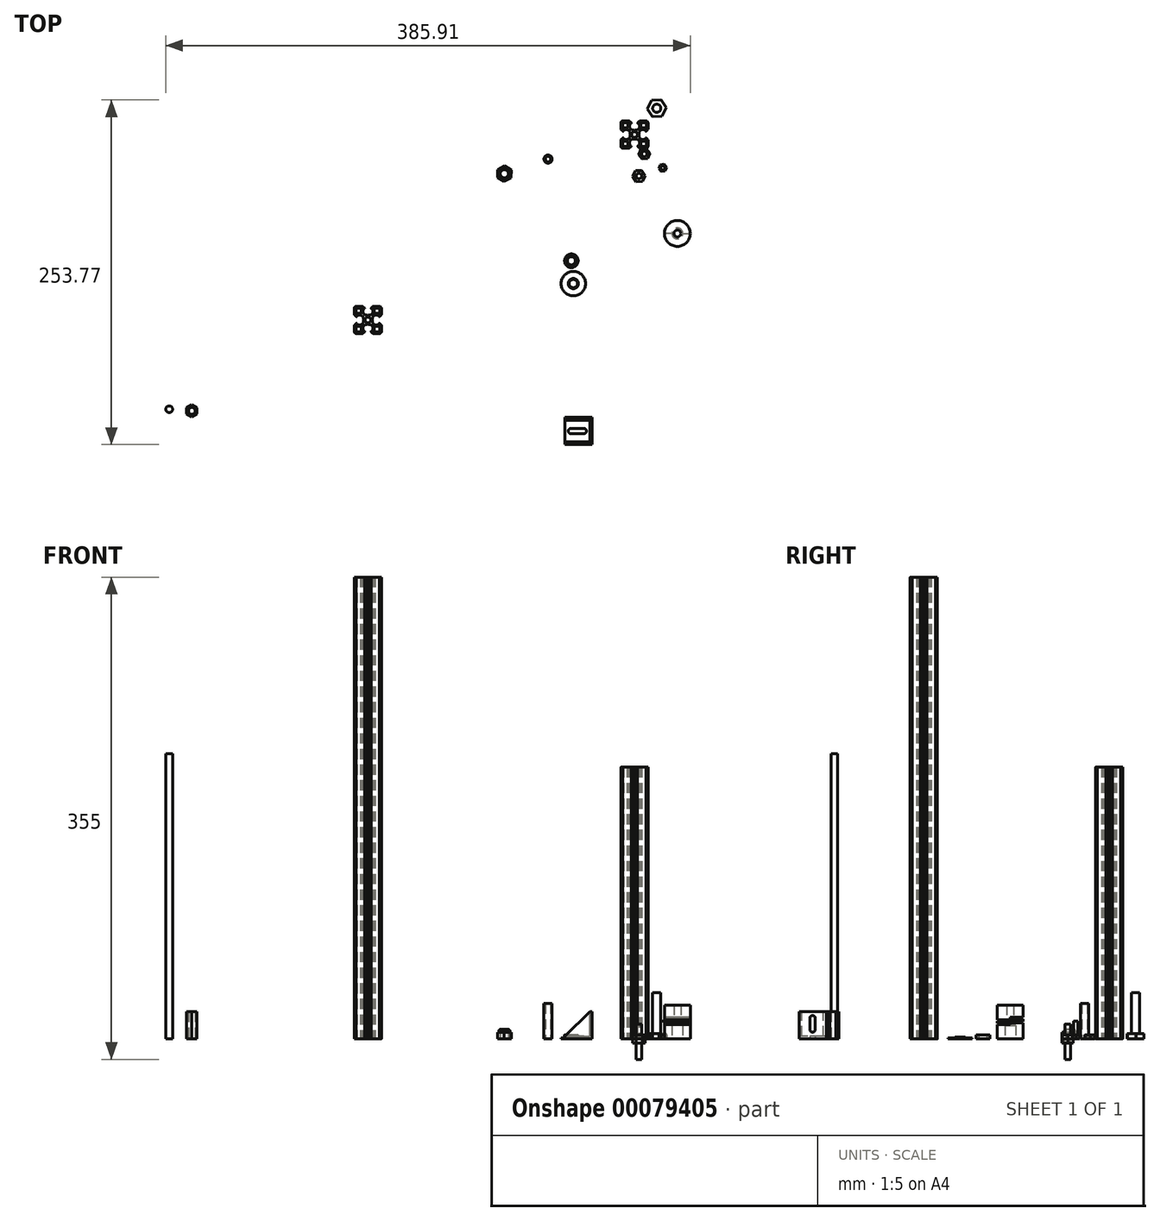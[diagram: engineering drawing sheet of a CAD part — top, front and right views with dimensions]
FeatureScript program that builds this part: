
annotation { "Feature Type Name" : "Feature", "Feature Type Description" : "" }
export const myFeature = defineFeature(function(context is Context, id is Id, definition is map)
    precondition{}
    {
        {
            var Q0;
            Q0=qCreatedBy(makeId("Top.planeOp"),FACE);
            var sketch = newSketch(context, id + "F0", { "sketchPlane" : qUnion([Q0])});
            skLineSegment(sketch, "E0", {"start": v(-9.77, 3.7) * mm, "end": v(-8.49, 2.4) * mm});
            skArc(sketch, "E1", {"start": v(-8.49, 2.4) * mm, "mid": v(-8.27, 2.36) * mm, "end": v(-8.14, 2.54) * mm});
            skLineSegment(sketch, "E2", {"start": v(-8.14, 2.54) * mm, "end": v(-8.14, 3.6) * mm});
            skLineSegment(sketch, "E3", {"start": v(-8.14, 3.6) * mm, "end": v(-5.03, 3.6) * mm});
            skLineSegment(sketch, "E4", {"start": v(-5.03, 3.6) * mm, "end": v(-3.4, 1.97) * mm});
            skLineSegment(sketch, "E5", {"start": v(-3.4, 1.97) * mm, "end": v(-3.4, 0.38) * mm});
            skLineSegment(sketch, "E6", {"start": v(-3.4, 0.38) * mm, "end": v(-3.02, 0) * mm});
            skLineSegment(sketch, "E7", {"start": v(-3.4, -0.38) * mm, "end": v(-3.02, 0) * mm});
            skLineSegment(sketch, "E8", {"start": v(-3.4, -1.97) * mm, "end": v(-3.4, -0.38) * mm});
            skLineSegment(sketch, "E9", {"start": v(-5.03, -3.6) * mm, "end": v(-3.4, -1.97) * mm});
            skLineSegment(sketch, "E10", {"start": v(-8.14, -3.6) * mm, "end": v(-5.03, -3.6) * mm});
            skLineSegment(sketch, "E11", {"start": v(-8.14, -2.54) * mm, "end": v(-8.14, -3.6) * mm});
            skArc(sketch, "E12", {"start": v(-8.49, -2.4) * mm, "mid": v(-8.27, -2.36) * mm, "end": v(-8.14, -2.54) * mm});
            skLineSegment(sketch, "E13", {"start": v(-9.77, -3.7) * mm, "end": v(-8.49, -2.4) * mm});
            skArc(sketch, "E14", {"start": v(-10, -4.25) * mm, "mid": v(-9.94, -3.95) * mm, "end": v(-9.77, -3.7) * mm});
            skLineSegment(sketch, "E15", {"start": v(-10, -8.58) * mm, "end": v(-10, -4.25) * mm});
            skArc(sketch, "E16", {"start": v(-8.6, -10) * mm, "mid": v(-9.57, -9.56) * mm, "end": v(-10, -8.58) * mm});
            skLineSegment(sketch, "E17", {"start": v(-4.04, -10) * mm, "end": v(-8.6, -10) * mm});
            skArc(sketch, "E18", {"start": v(-3.48, -9.77) * mm, "mid": v(-3.74, -9.94) * mm, "end": v(-4.04, -10) * mm});
            skLineSegment(sketch, "E19", {"start": v(-2.37, -8.66) * mm, "end": v(-3.48, -9.77) * mm});
            skArc(sketch, "E20", {"start": v(-2.55, -8.23) * mm, "mid": v(-2.32, -8.39) * mm, "end": v(-2.37, -8.66) * mm});
            skLineSegment(sketch, "E21", {"start": v(-3.6, -8.23) * mm, "end": v(-2.55, -8.23) * mm});
            skLineSegment(sketch, "E22", {"start": v(-3.6, -5.03) * mm, "end": v(-3.6, -8.23) * mm});
            skLineSegment(sketch, "E23", {"start": v(-2, -3.43) * mm, "end": v(-3.6, -5.03) * mm});
            skLineSegment(sketch, "E24", {"start": v(-0.3, -3.43) * mm, "end": v(-2, -3.43) * mm});
            skLineSegment(sketch, "E25", {"start": v(0, -3.18) * mm, "end": v(-0.3, -3.43) * mm});
            skLineSegment(sketch, "E26", {"start": v(0, -3.18) * mm, "end": v(0.3, -3.43) * mm});
            skLineSegment(sketch, "E27", {"start": v(0.3, -3.43) * mm, "end": v(2, -3.43) * mm});
            skLineSegment(sketch, "E28", {"start": v(2, -3.43) * mm, "end": v(3.6, -5.03) * mm});
            skLineSegment(sketch, "E29", {"start": v(3.6, -5.03) * mm, "end": v(3.6, -8.23) * mm});
            skLineSegment(sketch, "E30", {"start": v(3.6, -8.23) * mm, "end": v(2.55, -8.23) * mm});
            skArc(sketch, "E31", {"start": v(2.55, -8.23) * mm, "mid": v(2.32, -8.39) * mm, "end": v(2.37, -8.66) * mm});
            skLineSegment(sketch, "E32", {"start": v(2.37, -8.66) * mm, "end": v(3.48, -9.77) * mm});
            skArc(sketch, "E33", {"start": v(3.48, -9.77) * mm, "mid": v(3.74, -9.94) * mm, "end": v(4.04, -10) * mm});
            skLineSegment(sketch, "E34", {"start": v(4.04, -10) * mm, "end": v(8.6, -10) * mm});
            skArc(sketch, "E35", {"start": v(8.6, -10) * mm, "mid": v(9.57, -9.56) * mm, "end": v(10, -8.58) * mm});
            skLineSegment(sketch, "E36", {"start": v(10, -8.58) * mm, "end": v(10, -4.25) * mm});
            skArc(sketch, "E37", {"start": v(10, -4.25) * mm, "mid": v(9.94, -3.95) * mm, "end": v(9.77, -3.7) * mm});
            skLineSegment(sketch, "E38", {"start": v(9.77, -3.7) * mm, "end": v(8.49, -2.4) * mm});
            skArc(sketch, "E39", {"start": v(8.49, -2.4) * mm, "mid": v(8.27, -2.36) * mm, "end": v(8.14, -2.54) * mm});
            skLineSegment(sketch, "E40", {"start": v(8.14, -2.54) * mm, "end": v(8.14, -3.6) * mm});
            skLineSegment(sketch, "E41", {"start": v(8.14, -3.6) * mm, "end": v(5.03, -3.6) * mm});
            skLineSegment(sketch, "E42", {"start": v(5.03, -3.6) * mm, "end": v(3.4, -1.97) * mm});
            skLineSegment(sketch, "E43", {"start": v(3.4, -1.97) * mm, "end": v(3.4, -0.38) * mm});
            skLineSegment(sketch, "E44", {"start": v(3.4, -0.38) * mm, "end": v(3.02, 0) * mm});
            skLineSegment(sketch, "E45", {"start": v(3.4, 0.38) * mm, "end": v(3.02, 0) * mm});
            skLineSegment(sketch, "E46", {"start": v(3.4, 1.97) * mm, "end": v(3.4, 0.38) * mm});
            skLineSegment(sketch, "E47", {"start": v(5.03, 3.6) * mm, "end": v(3.4, 1.97) * mm});
            skLineSegment(sketch, "E48", {"start": v(8.14, 3.6) * mm, "end": v(5.03, 3.6) * mm});
            skLineSegment(sketch, "E49", {"start": v(8.14, 2.54) * mm, "end": v(8.14, 3.6) * mm});
            skArc(sketch, "E50", {"start": v(8.49, 2.4) * mm, "mid": v(8.27, 2.36) * mm, "end": v(8.14, 2.54) * mm});
            skLineSegment(sketch, "E51", {"start": v(9.77, 3.7) * mm, "end": v(8.49, 2.4) * mm});
            skArc(sketch, "E52", {"start": v(10, 4.25) * mm, "mid": v(9.94, 3.95) * mm, "end": v(9.77, 3.7) * mm});
            skLineSegment(sketch, "E53", {"start": v(10, 8.58) * mm, "end": v(10, 4.25) * mm});
            skArc(sketch, "E54", {"start": v(8.6, 10) * mm, "mid": v(9.57, 9.56) * mm, "end": v(10, 8.58) * mm});
            skLineSegment(sketch, "E55", {"start": v(4.04, 10) * mm, "end": v(8.6, 10) * mm});
            skArc(sketch, "E56", {"start": v(3.48, 9.77) * mm, "mid": v(3.74, 9.94) * mm, "end": v(4.04, 10) * mm});
            skLineSegment(sketch, "E57", {"start": v(2.37, 8.66) * mm, "end": v(3.48, 9.77) * mm});
            skArc(sketch, "E58", {"start": v(2.55, 8.23) * mm, "mid": v(2.32, 8.39) * mm, "end": v(2.37, 8.66) * mm});
            skLineSegment(sketch, "E59", {"start": v(3.6, 8.23) * mm, "end": v(2.55, 8.23) * mm});
            skLineSegment(sketch, "E60", {"start": v(3.6, 5.03) * mm, "end": v(3.6, 8.23) * mm});
            skLineSegment(sketch, "E61", {"start": v(2, 3.43) * mm, "end": v(3.6, 5.03) * mm});
            skLineSegment(sketch, "E62", {"start": v(0.3, 3.43) * mm, "end": v(2, 3.43) * mm});
            skLineSegment(sketch, "E63", {"start": v(0, 3.18) * mm, "end": v(0.3, 3.43) * mm});
            skLineSegment(sketch, "E64", {"start": v(0, 3.18) * mm, "end": v(-0.3, 3.43) * mm});
            skLineSegment(sketch, "E65", {"start": v(-0.3, 3.43) * mm, "end": v(-2, 3.43) * mm});
            skLineSegment(sketch, "E66", {"start": v(-2, 3.43) * mm, "end": v(-3.6, 5.03) * mm});
            skLineSegment(sketch, "E67", {"start": v(-3.6, 5.03) * mm, "end": v(-3.6, 8.23) * mm});
            skLineSegment(sketch, "E68", {"start": v(-3.6, 8.23) * mm, "end": v(-2.55, 8.23) * mm});
            skArc(sketch, "E69", {"start": v(-2.55, 8.23) * mm, "mid": v(-2.32, 8.39) * mm, "end": v(-2.37, 8.66) * mm});
            skLineSegment(sketch, "E70", {"start": v(-2.37, 8.66) * mm, "end": v(-3.48, 9.77) * mm});
            skArc(sketch, "E71", {"start": v(-3.48, 9.77) * mm, "mid": v(-3.74, 9.94) * mm, "end": v(-4.04, 10) * mm});
            skLineSegment(sketch, "E72", {"start": v(-4.04, 10) * mm, "end": v(-8.6, 10) * mm});
            skArc(sketch, "E73", {"start": v(-8.6, 10) * mm, "mid": v(-9.57, 9.56) * mm, "end": v(-10, 8.58) * mm});
            skLineSegment(sketch, "E74", {"start": v(-10, 8.58) * mm, "end": v(-10, 4.25) * mm});
            skArc(sketch, "E75", {"start": v(-10, 4.25) * mm, "mid": v(-9.94, 3.95) * mm, "end": v(-9.77, 3.7) * mm});
            skLineSegment(sketch, "E76", {"start": v(-8.8, -5.38) * mm, "end": v(-8.8, -8.38) * mm});
            skArc(sketch, "E77", {"start": v(-8.8, -5.38) * mm, "mid": v(-8.72, -5) * mm, "end": v(-8.39, -4.8) * mm});
            skLineSegment(sketch, "E78", {"start": v(-5.39, -4.8) * mm, "end": v(-8.39, -4.8) * mm});
            skArc(sketch, "E79", {"start": v(-5.39, -4.8) * mm, "mid": v(-4.94, -4.93) * mm, "end": v(-4.8, -5.38) * mm});
            skLineSegment(sketch, "E80", {"start": v(-4.8, -8.38) * mm, "end": v(-4.8, -5.38) * mm});
            skArc(sketch, "E81", {"start": v(-4.8, -8.38) * mm, "mid": v(-5, -8.72) * mm, "end": v(-5.4, -8.8) * mm});
            skLineSegment(sketch, "E82", {"start": v(-8.4, -8.8) * mm, "end": v(-5.4, -8.8) * mm});
            skArc(sketch, "E83", {"start": v(-8.4, -8.8) * mm, "mid": v(-8.67, -8.65) * mm, "end": v(-8.8, -8.38) * mm});
            skLineSegment(sketch, "E84", {"start": v(8.8, 5.38) * mm, "end": v(8.8, 8.38) * mm});
            skArc(sketch, "E85", {"start": v(8.8, 5.38) * mm, "mid": v(8.72, 5) * mm, "end": v(8.39, 4.8) * mm});
            skLineSegment(sketch, "E86", {"start": v(5.4, 4.93) * mm, "end": v(5.39, 4.8) * mm});
            skArc(sketch, "E87", {"start": v(5.39, 4.8) * mm, "mid": v(4.94, 4.93) * mm, "end": v(4.8, 5.38) * mm});
            skLineSegment(sketch, "E88", {"start": v(4.8, 8.38) * mm, "end": v(4.8, 5.38) * mm});
            skArc(sketch, "E89", {"start": v(4.8, 8.38) * mm, "mid": v(5, 8.72) * mm, "end": v(5.4, 8.8) * mm});
            skLineSegment(sketch, "E90", {"start": v(8.4, 8.8) * mm, "end": v(5.4, 8.8) * mm});
            skArc(sketch, "E91", {"start": v(8.4, 8.8) * mm, "mid": v(8.67, 8.65) * mm, "end": v(8.8, 8.38) * mm});
            skArc(sketch, "E92", {"start": v(5.39, -4.8) * mm, "mid": v(4.94, -4.93) * mm, "end": v(4.8, -5.38) * mm});
            skLineSegment(sketch, "E93", {"start": v(5.39, -4.8) * mm, "end": v(8.39, -4.8) * mm});
            skArc(sketch, "E94", {"start": v(8.8, -5.38) * mm, "mid": v(8.72, -5) * mm, "end": v(8.39, -4.8) * mm});
            skLineSegment(sketch, "E95", {"start": v(8.8, -5.38) * mm, "end": v(8.8, -8.38) * mm});
            skArc(sketch, "E96", {"start": v(8.4, -8.8) * mm, "mid": v(8.67, -8.65) * mm, "end": v(8.8, -8.38) * mm});
            skLineSegment(sketch, "E97", {"start": v(8.4, -8.8) * mm, "end": v(5.4, -8.8) * mm});
            skArc(sketch, "E98", {"start": v(4.8, -8.38) * mm, "mid": v(5, -8.72) * mm, "end": v(5.4, -8.8) * mm});
            skLineSegment(sketch, "E99", {"start": v(4.8, -8.38) * mm, "end": v(4.8, -5.38) * mm});
            skCircle(sketch, "E100", {"center": v(0, 0) * mm, "radius": 2.1 * mm});
            skArc(sketch, "E101", {"start": v(-5.39, 4.8) * mm, "mid": v(-4.94, 4.93) * mm, "end": v(-4.8, 5.38) * mm});
            skLineSegment(sketch, "E102", {"start": v(-5.39, 4.8) * mm, "end": v(-8.39, 4.8) * mm});
            skArc(sketch, "E103", {"start": v(-8.8, 5.38) * mm, "mid": v(-8.72, 5) * mm, "end": v(-8.39, 4.8) * mm});
            skLineSegment(sketch, "E104", {"start": v(-8.8, 5.38) * mm, "end": v(-8.8, 8.38) * mm});
            skArc(sketch, "E105", {"start": v(-8.4, 8.8) * mm, "mid": v(-8.67, 8.65) * mm, "end": v(-8.8, 8.38) * mm});
            skLineSegment(sketch, "E106", {"start": v(-8.4, 8.8) * mm, "end": v(-5.4, 8.8) * mm});
            skArc(sketch, "E107", {"start": v(-4.8, 8.38) * mm, "mid": v(-5, 8.72) * mm, "end": v(-5.4, 8.8) * mm});
            skLineSegment(sketch, "E108", {"start": v(-4.8, 8.38) * mm, "end": v(-4.8, 5.38) * mm});
            skLineSegment(sketch, "E109", {"start": v(89.28, 71.86) * mm, "end": v(92.28, 71.86) * mm});
            skLineSegment(sketch, "E110", {"start": v(106.08, 71.86) * mm, "end": v(103.08, 71.86) * mm});
            skLineSegment(sketch, "E111", {"start": v(87.68, 71.65) * mm, "end": v(87.68, 67.31) * mm});
            skLineSegment(sketch, "E112", {"start": v(107.68, 71.65) * mm, "end": v(107.68, 67.31) * mm});
            skArc(sketch, "E113", {"start": v(106.08, 71.86) * mm, "mid": v(106.35, 71.72) * mm, "end": v(106.48, 71.45) * mm});
            skLineSegment(sketch, "E114", {"start": v(103.07, 67.86) * mm, "end": v(106.07, 67.86) * mm});
            skLineSegment(sketch, "E115", {"start": v(93.64, 53.06) * mm, "end": v(89.08, 53.06) * mm});
            skLineSegment(sketch, "E116", {"start": v(101.73, 73.06) * mm, "end": v(106.28, 73.06) * mm});
            skArc(sketch, "E117", {"start": v(94.2, 53.3) * mm, "mid": v(93.95, 53.13) * mm, "end": v(93.64, 53.06) * mm});
            skLineSegment(sketch, "E118", {"start": v(89.28, 54.26) * mm, "end": v(92.28, 54.26) * mm});
            skLineSegment(sketch, "E119", {"start": v(87.91, 59.37) * mm, "end": v(89.2, 60.66) * mm});
            skArc(sketch, "E120", {"start": v(87.68, 58.82) * mm, "mid": v(87.74, 59.12) * mm, "end": v(87.91, 59.37) * mm});
            skLineSegment(sketch, "E121", {"start": v(87.68, 54.48) * mm, "end": v(87.68, 58.82) * mm});
            skLineSegment(sketch, "E122", {"start": v(87.91, 66.76) * mm, "end": v(89.2, 65.47) * mm});
            skArc(sketch, "E123", {"start": v(89.08, 53.06) * mm, "mid": v(88.11, 53.5) * mm, "end": v(87.68, 54.48) * mm});
            skLineSegment(sketch, "E124", {"start": v(92.88, 54.68) * mm, "end": v(92.88, 57.68) * mm});
            skLineSegment(sketch, "E125", {"start": v(105.83, 66.66) * mm, "end": v(102.71, 66.66) * mm});
            skLineSegment(sketch, "E126", {"start": v(93.64, 73.06) * mm, "end": v(89.08, 73.06) * mm});
            skLineSegment(sketch, "E127", {"start": v(100.06, 71.73) * mm, "end": v(101.16, 72.83) * mm});
            skLineSegment(sketch, "E128", {"start": v(94.08, 68.1) * mm, "end": v(94.08, 71.3) * mm});
            skLineSegment(sketch, "E129", {"start": v(107.45, 66.76) * mm, "end": v(106.17, 65.47) * mm});
            skLineSegment(sketch, "E130", {"start": v(106.48, 68.45) * mm, "end": v(106.48, 71.45) * mm});
            skArc(sketch, "E131", {"start": v(88.88, 57.68) * mm, "mid": v(88.97, 58.06) * mm, "end": v(89.3, 58.26) * mm});
            skLineSegment(sketch, "E132", {"start": v(94.08, 58.03) * mm, "end": v(94.08, 54.83) * mm});
            skLineSegment(sketch, "E133", {"start": v(95.3, 71.73) * mm, "end": v(94.2, 72.83) * mm});
            skLineSegment(sketch, "E134", {"start": v(92.88, 71.45) * mm, "end": v(92.88, 68.45) * mm});
            skLineSegment(sketch, "E135", {"start": v(88.88, 57.68) * mm, "end": v(88.88, 54.68) * mm});
            skLineSegment(sketch, "E136", {"start": v(89.54, 66.66) * mm, "end": v(92.65, 66.66) * mm});
            skLineSegment(sketch, "E137", {"start": v(89.54, 59.46) * mm, "end": v(92.65, 59.46) * mm});
            skLineSegment(sketch, "E138", {"start": v(89.54, 60.52) * mm, "end": v(89.54, 59.46) * mm});
            skArc(sketch, "E139", {"start": v(102.48, 71.45) * mm, "mid": v(102.7, 71.79) * mm, "end": v(103.08, 71.86) * mm});
            skArc(sketch, "E140", {"start": v(95.13, 54.83) * mm, "mid": v(95.36, 54.68) * mm, "end": v(95.3, 54.4) * mm});
            skLineSegment(sketch, "E141", {"start": v(94.08, 54.83) * mm, "end": v(95.13, 54.83) * mm});
            skArc(sketch, "E142", {"start": v(92.3, 67.86) * mm, "mid": v(92.74, 68) * mm, "end": v(92.88, 68.45) * mm});
            skLineSegment(sketch, "E143", {"start": v(92.3, 58.26) * mm, "end": v(89.3, 58.26) * mm});
            skLineSegment(sketch, "E144", {"start": v(92.65, 59.46) * mm, "end": v(94.28, 61.1) * mm});
            skLineSegment(sketch, "E145", {"start": v(88.88, 68.45) * mm, "end": v(88.88, 71.45) * mm});
            skLineSegment(sketch, "E146", {"start": v(102.48, 71.45) * mm, "end": v(102.48, 68.45) * mm});
            skArc(sketch, "E147", {"start": v(106.28, 53.06) * mm, "mid": v(107.25, 53.5) * mm, "end": v(107.68, 54.48) * mm});
            skLineSegment(sketch, "E148", {"start": v(107.68, 54.48) * mm, "end": v(107.68, 58.82) * mm});
            skCircle(sketch, "E149", {"center": v(97.68, 63.06) * mm, "radius": 2.1 * mm});
            skLineSegment(sketch, "E150", {"start": v(103.07, 58.26) * mm, "end": v(106.07, 58.26) * mm});
            skLineSegment(sketch, "E151", {"start": v(107.45, 59.37) * mm, "end": v(106.17, 60.66) * mm});
            skLineSegment(sketch, "E152", {"start": v(92.3, 67.86) * mm, "end": v(89.3, 67.86) * mm});
            skLineSegment(sketch, "E153", {"start": v(101.28, 68.1) * mm, "end": v(101.28, 71.3) * mm});
            skLineSegment(sketch, "E154", {"start": v(95.68, 59.63) * mm, "end": v(94.08, 58.03) * mm});
            skLineSegment(sketch, "E155", {"start": v(97.38, 66.5) * mm, "end": v(95.68, 66.5) * mm});
            skLineSegment(sketch, "E156", {"start": v(106.08, 54.26) * mm, "end": v(103.08, 54.26) * mm});
            skArc(sketch, "E157", {"start": v(103.07, 58.26) * mm, "mid": v(102.62, 58.13) * mm, "end": v(102.48, 57.68) * mm});
            skLineSegment(sketch, "E158", {"start": v(97.98, 66.5) * mm, "end": v(99.69, 66.5) * mm});
            skLineSegment(sketch, "E159", {"start": v(101.08, 65.03) * mm, "end": v(101.08, 63.45) * mm});
            skLineSegment(sketch, "E160", {"start": v(95.68, 66.5) * mm, "end": v(94.08, 68.1) * mm});
            skLineSegment(sketch, "E161", {"start": v(101.73, 53.06) * mm, "end": v(106.28, 53.06) * mm});
            skArc(sketch, "E162", {"start": v(102.48, 54.68) * mm, "mid": v(102.7, 54.34) * mm, "end": v(103.08, 54.26) * mm});
            skLineSegment(sketch, "E163", {"start": v(102.71, 66.66) * mm, "end": v(101.08, 65.03) * mm});
            skLineSegment(sketch, "E164", {"start": v(106.48, 57.68) * mm, "end": v(106.48, 54.68) * mm});
            skLineSegment(sketch, "E165", {"start": v(92.65, 66.66) * mm, "end": v(94.28, 65.03) * mm});
            skLineSegment(sketch, "E166", {"start": v(94.28, 65.03) * mm, "end": v(94.28, 63.45) * mm});
            skLineSegment(sketch, "E167", {"start": v(94.28, 61.1) * mm, "end": v(94.28, 62.68) * mm});
            skLineSegment(sketch, "E168", {"start": v(97.68, 59.89) * mm, "end": v(97.98, 59.63) * mm});
            skLineSegment(sketch, "E169", {"start": v(101.28, 71.3) * mm, "end": v(100.23, 71.3) * mm});
            skLineSegment(sketch, "E170", {"start": v(101.08, 61.1) * mm, "end": v(101.08, 62.68) * mm});
            skLineSegment(sketch, "E171", {"start": v(99.69, 66.5) * mm, "end": v(101.28, 68.1) * mm});
            skLineSegment(sketch, "E172", {"start": v(101.08, 63.45) * mm, "end": v(100.7, 63.06) * mm});
            skLineSegment(sketch, "E173", {"start": v(101.28, 58.03) * mm, "end": v(101.28, 54.83) * mm});
            skArc(sketch, "E174", {"start": v(103.07, 67.86) * mm, "mid": v(102.62, 68) * mm, "end": v(102.48, 68.45) * mm});
            skLineSegment(sketch, "E175", {"start": v(101.28, 54.83) * mm, "end": v(100.23, 54.83) * mm});
            skLineSegment(sketch, "E176", {"start": v(105.83, 59.46) * mm, "end": v(102.71, 59.46) * mm});
            skLineSegment(sketch, "E177", {"start": v(97.68, 59.89) * mm, "end": v(97.38, 59.63) * mm});
            skLineSegment(sketch, "E178", {"start": v(102.48, 54.68) * mm, "end": v(102.48, 57.68) * mm});
            skLineSegment(sketch, "E179", {"start": v(97.38, 59.63) * mm, "end": v(95.68, 59.63) * mm});
            skArc(sketch, "E180", {"start": v(100.23, 71.3) * mm, "mid": v(100, 71.45) * mm, "end": v(100.06, 71.73) * mm});
            skLineSegment(sketch, "E181", {"start": v(102.71, 59.46) * mm, "end": v(101.08, 61.1) * mm});
            skLineSegment(sketch, "E182", {"start": v(95.3, 54.4) * mm, "end": v(94.2, 53.3) * mm});
            skLineSegment(sketch, "E183", {"start": v(97.98, 59.63) * mm, "end": v(99.69, 59.63) * mm});
            skArc(sketch, "E184", {"start": v(89.08, 73.06) * mm, "mid": v(88.11, 72.62) * mm, "end": v(87.68, 71.65) * mm});
            skLineSegment(sketch, "E185", {"start": v(94.08, 71.3) * mm, "end": v(95.13, 71.3) * mm});
            skArc(sketch, "E186", {"start": v(107.68, 67.31) * mm, "mid": v(107.62, 67.01) * mm, "end": v(107.45, 66.76) * mm});
            skArc(sketch, "E187", {"start": v(106.48, 68.45) * mm, "mid": v(106.4, 68.07) * mm, "end": v(106.07, 67.86) * mm});
            skArc(sketch, "E188", {"start": v(107.68, 58.82) * mm, "mid": v(107.62, 59.12) * mm, "end": v(107.45, 59.37) * mm});
            skArc(sketch, "E189", {"start": v(92.88, 71.45) * mm, "mid": v(92.67, 71.79) * mm, "end": v(92.28, 71.86) * mm});
            skArc(sketch, "E190", {"start": v(87.68, 67.31) * mm, "mid": v(87.74, 67.01) * mm, "end": v(87.91, 66.76) * mm});
            skArc(sketch, "E191", {"start": v(106.28, 73.06) * mm, "mid": v(107.25, 72.62) * mm, "end": v(107.68, 71.65) * mm});
            skArc(sketch, "E192", {"start": v(92.88, 54.68) * mm, "mid": v(92.67, 54.34) * mm, "end": v(92.28, 54.26) * mm});
            skLineSegment(sketch, "E193", {"start": v(101.08, 62.68) * mm, "end": v(100.7, 63.06) * mm});
            skLineSegment(sketch, "E194", {"start": v(99.69, 59.63) * mm, "end": v(101.28, 58.03) * mm});
            skArc(sketch, "E195", {"start": v(88.88, 68.45) * mm, "mid": v(88.97, 68.07) * mm, "end": v(89.3, 67.86) * mm});
            skArc(sketch, "E196", {"start": v(101.16, 53.3) * mm, "mid": v(101.42, 53.13) * mm, "end": v(101.73, 53.06) * mm});
            skArc(sketch, "E197", {"start": v(94.2, 72.83) * mm, "mid": v(93.95, 73) * mm, "end": v(93.64, 73.06) * mm});
            skArc(sketch, "E198", {"start": v(106.48, 57.68) * mm, "mid": v(106.4, 58.06) * mm, "end": v(106.07, 58.26) * mm});
            skArc(sketch, "E199", {"start": v(92.3, 58.26) * mm, "mid": v(92.74, 58.13) * mm, "end": v(92.88, 57.68) * mm});
            skLineSegment(sketch, "E200", {"start": v(97.68, 66.24) * mm, "end": v(97.98, 66.5) * mm});
            skArc(sketch, "E201", {"start": v(100.23, 54.83) * mm, "mid": v(100, 54.68) * mm, "end": v(100.06, 54.4) * mm});
            skLineSegment(sketch, "E202", {"start": v(89.54, 65.6) * mm, "end": v(89.54, 66.66) * mm});
            skLineSegment(sketch, "E203", {"start": v(94.28, 63.45) * mm, "end": v(94.66, 63.06) * mm});
            skLineSegment(sketch, "E204", {"start": v(94.28, 62.68) * mm, "end": v(94.66, 63.06) * mm});
            skArc(sketch, "E205", {"start": v(89.2, 60.66) * mm, "mid": v(89.41, 60.7) * mm, "end": v(89.54, 60.52) * mm});
            skArc(sketch, "E206", {"start": v(106.08, 54.26) * mm, "mid": v(106.35, 54.41) * mm, "end": v(106.48, 54.68) * mm});
            skLineSegment(sketch, "E207", {"start": v(97.68, 66.24) * mm, "end": v(97.38, 66.5) * mm});
            skLineSegment(sketch, "E208", {"start": v(100.06, 54.4) * mm, "end": v(101.16, 53.3) * mm});
            skArc(sketch, "E209", {"start": v(101.16, 72.83) * mm, "mid": v(101.42, 73) * mm, "end": v(101.73, 73.06) * mm});
            skLineSegment(sketch, "E210", {"start": v(105.83, 60.52) * mm, "end": v(105.83, 59.46) * mm});
            skArc(sketch, "E211", {"start": v(89.28, 54.26) * mm, "mid": v(89.02, 54.41) * mm, "end": v(88.88, 54.68) * mm});
            skArc(sketch, "E212", {"start": v(95.13, 71.3) * mm, "mid": v(95.36, 71.45) * mm, "end": v(95.3, 71.73) * mm});
            skArc(sketch, "E213", {"start": v(106.17, 60.66) * mm, "mid": v(105.96, 60.7) * mm, "end": v(105.83, 60.52) * mm});
            skLineSegment(sketch, "E214", {"start": v(105.83, 65.6) * mm, "end": v(105.83, 66.66) * mm});
            skArc(sketch, "E215", {"start": v(106.17, 65.47) * mm, "mid": v(105.96, 65.43) * mm, "end": v(105.83, 65.6) * mm});
            skArc(sketch, "E216", {"start": v(89.2, 65.47) * mm, "mid": v(89.41, 65.43) * mm, "end": v(89.54, 65.6) * mm});
            skArc(sketch, "E217", {"start": v(89.28, 71.86) * mm, "mid": v(89.02, 71.72) * mm, "end": v(88.88, 71.45) * mm});
            skLineSegment(sketch, "E218", {"start": v(121.74, 81.59) * mm, "end": v(124.74, 81.59) * mm});
            skLineSegment(sketch, "E219", {"start": v(138.53, 81.59) * mm, "end": v(135.53, 81.59) * mm});
            skLineSegment(sketch, "E220", {"start": v(120.14, 81.37) * mm, "end": v(120.14, 77.04) * mm});
            skLineSegment(sketch, "E221", {"start": v(140.14, 81.37) * mm, "end": v(140.14, 77.04) * mm});
            skArc(sketch, "E222", {"start": v(138.53, 81.59) * mm, "mid": v(138.8, 81.44) * mm, "end": v(138.94, 81.17) * mm});
            skLineSegment(sketch, "E223", {"start": v(135.52, 77.59) * mm, "end": v(138.52, 77.59) * mm});
            skLineSegment(sketch, "E224", {"start": v(126.1, 62.79) * mm, "end": v(121.54, 62.79) * mm});
            skLineSegment(sketch, "E225", {"start": v(134.18, 82.79) * mm, "end": v(138.73, 82.79) * mm});
            skArc(sketch, "E226", {"start": v(126.66, 63.02) * mm, "mid": v(126.4, 62.85) * mm, "end": v(126.1, 62.79) * mm});
            skLineSegment(sketch, "E227", {"start": v(121.74, 63.99) * mm, "end": v(124.74, 63.99) * mm});
            skLineSegment(sketch, "E228", {"start": v(120.37, 69.1) * mm, "end": v(121.65, 70.38) * mm});
            skArc(sketch, "E229", {"start": v(120.14, 68.54) * mm, "mid": v(120.2, 68.84) * mm, "end": v(120.37, 69.1) * mm});
            skLineSegment(sketch, "E230", {"start": v(120.14, 64.2) * mm, "end": v(120.14, 68.54) * mm});
            skLineSegment(sketch, "E231", {"start": v(120.37, 76.48) * mm, "end": v(121.65, 75.2) * mm});
            skArc(sketch, "E232", {"start": v(121.54, 62.79) * mm, "mid": v(120.57, 63.23) * mm, "end": v(120.14, 64.2) * mm});
            skLineSegment(sketch, "E233", {"start": v(125.34, 64.4) * mm, "end": v(125.34, 67.4) * mm});
            skLineSegment(sketch, "E234", {"start": v(138.28, 76.39) * mm, "end": v(135.16, 76.39) * mm});
            skLineSegment(sketch, "E235", {"start": v(126.1, 82.79) * mm, "end": v(121.54, 82.79) * mm});
            skLineSegment(sketch, "E236", {"start": v(132.5, 81.45) * mm, "end": v(133.61, 82.55) * mm});
            skLineSegment(sketch, "E237", {"start": v(126.54, 77.82) * mm, "end": v(126.54, 81.02) * mm});
            skLineSegment(sketch, "E238", {"start": v(139.9, 76.48) * mm, "end": v(138.62, 75.2) * mm});
            skLineSegment(sketch, "E239", {"start": v(138.94, 78.17) * mm, "end": v(138.94, 81.17) * mm});
            skArc(sketch, "E240", {"start": v(121.34, 67.4) * mm, "mid": v(121.42, 67.78) * mm, "end": v(121.75, 67.99) * mm});
            skLineSegment(sketch, "E241", {"start": v(126.54, 67.75) * mm, "end": v(126.54, 64.55) * mm});
            skLineSegment(sketch, "E242", {"start": v(127.76, 81.45) * mm, "end": v(126.66, 82.55) * mm});
            skLineSegment(sketch, "E243", {"start": v(125.34, 81.17) * mm, "end": v(125.34, 78.17) * mm});
            skLineSegment(sketch, "E244", {"start": v(121.34, 67.4) * mm, "end": v(121.34, 64.4) * mm});
            skLineSegment(sketch, "E245", {"start": v(122, 76.39) * mm, "end": v(125.1, 76.39) * mm});
            skLineSegment(sketch, "E246", {"start": v(122, 69.19) * mm, "end": v(125.1, 69.19) * mm});
            skLineSegment(sketch, "E247", {"start": v(122, 70.25) * mm, "end": v(122, 69.19) * mm});
            skArc(sketch, "E248", {"start": v(134.94, 81.17) * mm, "mid": v(135.14, 81.5) * mm, "end": v(135.53, 81.59) * mm});
            skArc(sketch, "E249", {"start": v(127.59, 64.55) * mm, "mid": v(127.82, 64.4) * mm, "end": v(127.76, 64.13) * mm});
            skLineSegment(sketch, "E250", {"start": v(126.54, 64.55) * mm, "end": v(127.59, 64.55) * mm});
            skArc(sketch, "E251", {"start": v(124.75, 77.59) * mm, "mid": v(125.2, 77.72) * mm, "end": v(125.34, 78.17) * mm});
            skLineSegment(sketch, "E252", {"start": v(124.75, 67.99) * mm, "end": v(121.75, 67.99) * mm});
            skLineSegment(sketch, "E253", {"start": v(125.1, 69.19) * mm, "end": v(126.74, 70.82) * mm});
            skLineSegment(sketch, "E254", {"start": v(121.34, 78.17) * mm, "end": v(121.34, 81.17) * mm});
            skLineSegment(sketch, "E255", {"start": v(134.94, 81.17) * mm, "end": v(134.94, 78.17) * mm});
            skArc(sketch, "E256", {"start": v(138.73, 62.79) * mm, "mid": v(139.7, 63.23) * mm, "end": v(140.14, 64.2) * mm});
            skLineSegment(sketch, "E257", {"start": v(140.14, 64.2) * mm, "end": v(140.14, 68.54) * mm});
            skCircle(sketch, "E258", {"center": v(130.14, 72.79) * mm, "radius": 2.1 * mm});
            skLineSegment(sketch, "E259", {"start": v(135.52, 67.99) * mm, "end": v(138.52, 67.99) * mm});
            skLineSegment(sketch, "E260", {"start": v(139.9, 69.1) * mm, "end": v(138.62, 70.38) * mm});
            skLineSegment(sketch, "E261", {"start": v(124.75, 77.59) * mm, "end": v(121.75, 77.59) * mm});
            skLineSegment(sketch, "E262", {"start": v(133.74, 77.82) * mm, "end": v(133.74, 81.02) * mm});
            skLineSegment(sketch, "E263", {"start": v(128.13, 69.35) * mm, "end": v(126.54, 67.75) * mm});
            skLineSegment(sketch, "E264", {"start": v(129.84, 76.22) * mm, "end": v(128.13, 76.22) * mm});
            skLineSegment(sketch, "E265", {"start": v(138.53, 63.99) * mm, "end": v(135.53, 63.99) * mm});
            skArc(sketch, "E266", {"start": v(135.52, 67.99) * mm, "mid": v(135.08, 67.85) * mm, "end": v(134.94, 67.4) * mm});
            skLineSegment(sketch, "E267", {"start": v(130.44, 76.22) * mm, "end": v(132.14, 76.22) * mm});
            skLineSegment(sketch, "E268", {"start": v(133.54, 74.75) * mm, "end": v(133.54, 73.17) * mm});
            skLineSegment(sketch, "E269", {"start": v(128.13, 76.22) * mm, "end": v(126.54, 77.82) * mm});
            skLineSegment(sketch, "E270", {"start": v(134.18, 62.79) * mm, "end": v(138.73, 62.79) * mm});
            skArc(sketch, "E271", {"start": v(134.94, 64.4) * mm, "mid": v(135.14, 64.07) * mm, "end": v(135.53, 63.99) * mm});
            skLineSegment(sketch, "E272", {"start": v(135.16, 76.39) * mm, "end": v(133.54, 74.75) * mm});
            skLineSegment(sketch, "E273", {"start": v(138.94, 67.4) * mm, "end": v(138.94, 64.4) * mm});
            skLineSegment(sketch, "E274", {"start": v(125.1, 76.39) * mm, "end": v(126.74, 74.75) * mm});
            skLineSegment(sketch, "E275", {"start": v(126.74, 74.75) * mm, "end": v(126.74, 73.17) * mm});
            skLineSegment(sketch, "E276", {"start": v(126.74, 70.82) * mm, "end": v(126.74, 72.4) * mm});
            skLineSegment(sketch, "E277", {"start": v(130.14, 69.61) * mm, "end": v(130.44, 69.35) * mm});
            skLineSegment(sketch, "E278", {"start": v(133.74, 81.02) * mm, "end": v(132.69, 81.02) * mm});
            skLineSegment(sketch, "E279", {"start": v(133.54, 70.82) * mm, "end": v(133.54, 72.4) * mm});
            skLineSegment(sketch, "E280", {"start": v(132.14, 76.22) * mm, "end": v(133.74, 77.82) * mm});
            skLineSegment(sketch, "E281", {"start": v(133.54, 73.17) * mm, "end": v(133.15, 72.79) * mm});
            skLineSegment(sketch, "E282", {"start": v(133.74, 67.75) * mm, "end": v(133.74, 64.55) * mm});
            skArc(sketch, "E283", {"start": v(135.52, 77.59) * mm, "mid": v(135.08, 77.72) * mm, "end": v(134.94, 78.17) * mm});
            skLineSegment(sketch, "E284", {"start": v(133.74, 64.55) * mm, "end": v(132.69, 64.55) * mm});
            skLineSegment(sketch, "E285", {"start": v(138.28, 69.19) * mm, "end": v(135.16, 69.19) * mm});
            skLineSegment(sketch, "E286", {"start": v(130.14, 69.61) * mm, "end": v(129.84, 69.35) * mm});
            skLineSegment(sketch, "E287", {"start": v(134.94, 64.4) * mm, "end": v(134.94, 67.4) * mm});
            skLineSegment(sketch, "E288", {"start": v(129.84, 69.35) * mm, "end": v(128.13, 69.35) * mm});
            skArc(sketch, "E289", {"start": v(132.69, 81.02) * mm, "mid": v(132.45, 81.18) * mm, "end": v(132.5, 81.45) * mm});
            skLineSegment(sketch, "E290", {"start": v(135.16, 69.19) * mm, "end": v(133.54, 70.82) * mm});
            skLineSegment(sketch, "E291", {"start": v(127.76, 64.13) * mm, "end": v(126.66, 63.02) * mm});
            skLineSegment(sketch, "E292", {"start": v(130.44, 69.35) * mm, "end": v(132.14, 69.35) * mm});
            skArc(sketch, "E293", {"start": v(121.54, 82.79) * mm, "mid": v(120.57, 82.35) * mm, "end": v(120.14, 81.37) * mm});
            skLineSegment(sketch, "E294", {"start": v(126.54, 81.02) * mm, "end": v(127.59, 81.02) * mm});
            skArc(sketch, "E295", {"start": v(140.14, 77.04) * mm, "mid": v(140.08, 76.74) * mm, "end": v(139.9, 76.48) * mm});
            skArc(sketch, "E296", {"start": v(138.94, 78.17) * mm, "mid": v(138.85, 77.8) * mm, "end": v(138.52, 77.59) * mm});
            skArc(sketch, "E297", {"start": v(140.14, 68.54) * mm, "mid": v(140.08, 68.84) * mm, "end": v(139.9, 69.1) * mm});
            skArc(sketch, "E298", {"start": v(125.34, 81.17) * mm, "mid": v(125.13, 81.5) * mm, "end": v(124.74, 81.59) * mm});
            skArc(sketch, "E299", {"start": v(120.14, 77.04) * mm, "mid": v(120.2, 76.74) * mm, "end": v(120.37, 76.48) * mm});
            skArc(sketch, "E300", {"start": v(138.73, 82.79) * mm, "mid": v(139.7, 82.35) * mm, "end": v(140.14, 81.37) * mm});
            skArc(sketch, "E301", {"start": v(125.34, 64.4) * mm, "mid": v(125.13, 64.07) * mm, "end": v(124.74, 63.99) * mm});
            skLineSegment(sketch, "E302", {"start": v(133.54, 72.4) * mm, "end": v(133.15, 72.79) * mm});
            skLineSegment(sketch, "E303", {"start": v(132.14, 69.35) * mm, "end": v(133.74, 67.75) * mm});
            skArc(sketch, "E304", {"start": v(121.34, 78.17) * mm, "mid": v(121.42, 77.8) * mm, "end": v(121.75, 77.59) * mm});
            skArc(sketch, "E305", {"start": v(133.61, 63.02) * mm, "mid": v(133.87, 62.85) * mm, "end": v(134.18, 62.79) * mm});
            skArc(sketch, "E306", {"start": v(126.66, 82.55) * mm, "mid": v(126.4, 82.73) * mm, "end": v(126.1, 82.79) * mm});
            skArc(sketch, "E307", {"start": v(138.94, 67.4) * mm, "mid": v(138.85, 67.78) * mm, "end": v(138.52, 67.99) * mm});
            skArc(sketch, "E308", {"start": v(124.75, 67.99) * mm, "mid": v(125.2, 67.85) * mm, "end": v(125.34, 67.4) * mm});
            skLineSegment(sketch, "E309", {"start": v(130.14, 75.96) * mm, "end": v(130.44, 76.22) * mm});
            skArc(sketch, "E310", {"start": v(132.69, 64.55) * mm, "mid": v(132.45, 64.4) * mm, "end": v(132.5, 64.13) * mm});
            skLineSegment(sketch, "E311", {"start": v(122, 75.33) * mm, "end": v(122, 76.39) * mm});
            skLineSegment(sketch, "E312", {"start": v(126.74, 73.17) * mm, "end": v(127.12, 72.79) * mm});
            skLineSegment(sketch, "E313", {"start": v(126.74, 72.4) * mm, "end": v(127.12, 72.79) * mm});
            skArc(sketch, "E314", {"start": v(121.65, 70.38) * mm, "mid": v(121.86, 70.43) * mm, "end": v(122, 70.25) * mm});
            skArc(sketch, "E315", {"start": v(138.53, 63.99) * mm, "mid": v(138.8, 64.13) * mm, "end": v(138.94, 64.4) * mm});
            skLineSegment(sketch, "E316", {"start": v(130.14, 75.96) * mm, "end": v(129.84, 76.22) * mm});
            skLineSegment(sketch, "E317", {"start": v(132.5, 64.13) * mm, "end": v(133.61, 63.02) * mm});
            skArc(sketch, "E318", {"start": v(133.61, 82.55) * mm, "mid": v(133.87, 82.73) * mm, "end": v(134.18, 82.79) * mm});
            skLineSegment(sketch, "E319", {"start": v(138.28, 70.25) * mm, "end": v(138.28, 69.19) * mm});
            skArc(sketch, "E320", {"start": v(121.74, 63.99) * mm, "mid": v(121.47, 64.13) * mm, "end": v(121.34, 64.4) * mm});
            skArc(sketch, "E321", {"start": v(127.59, 81.02) * mm, "mid": v(127.82, 81.18) * mm, "end": v(127.76, 81.45) * mm});
            skArc(sketch, "E322", {"start": v(138.62, 70.38) * mm, "mid": v(138.4, 70.43) * mm, "end": v(138.28, 70.25) * mm});
            skLineSegment(sketch, "E323", {"start": v(138.28, 75.33) * mm, "end": v(138.28, 76.39) * mm});
            skArc(sketch, "E324", {"start": v(138.62, 75.2) * mm, "mid": v(138.4, 75.15) * mm, "end": v(138.28, 75.33) * mm});
            skArc(sketch, "E325", {"start": v(121.65, 75.2) * mm, "mid": v(121.86, 75.15) * mm, "end": v(122, 75.33) * mm});
            skArc(sketch, "E326", {"start": v(121.74, 81.59) * mm, "mid": v(121.47, 81.44) * mm, "end": v(121.34, 81.17) * mm});
            skLineSegment(sketch, "E327", {"start": v(-31.83, 29.57) * mm, "end": v(-30.2, 31.2) * mm});
            skLineSegment(sketch, "E328", {"start": v(-30.2, 36.86) * mm, "end": v(-27.1, 36.86) * mm});
            skLineSegment(sketch, "E329", {"start": v(-27.1, 36.86) * mm, "end": v(-25.46, 35.23) * mm});
            skLineSegment(sketch, "E330", {"start": v(-27.1, 29.66) * mm, "end": v(-25.46, 31.3) * mm});
            skLineSegment(sketch, "E331", {"start": v(-30.2, 29.66) * mm, "end": v(-27.1, 29.66) * mm});
            skLineSegment(sketch, "E332", {"start": v(-31.83, 36.95) * mm, "end": v(-30.2, 35.33) * mm});
            skLineSegment(sketch, "E333", {"start": v(-30.2, 35.33) * mm, "end": v(-30.2, 36.86) * mm});
            skLineSegment(sketch, "E334", {"start": v(-25.46, 35.23) * mm, "end": v(-25.46, 33.64) * mm});
            skLineSegment(sketch, "E335", {"start": v(-25.46, 31.3) * mm, "end": v(-25.46, 32.88) * mm});
            skLineSegment(sketch, "E336", {"start": v(-30.2, 31.2) * mm, "end": v(-30.2, 29.66) * mm});
            skLineSegment(sketch, "E337", {"start": v(-25.46, 32.88) * mm, "end": v(-25.46, 33.64) * mm});
            skLineSegment(sketch, "E338.MirrorCS", {"start": v(-32.3, 29.57) * mm, "end": v(-33.92, 31.2) * mm});
            skLineSegment(sketch, "E339.MirrorCS", {"start": v(-32.3, 36.95) * mm, "end": v(-33.92, 35.33) * mm});
            skLineSegment(sketch, "E340.MirrorCS", {"start": v(-33.92, 35.33) * mm, "end": v(-33.92, 36.86) * mm});
            skLineSegment(sketch, "E341.MirrorCS", {"start": v(-33.92, 36.86) * mm, "end": v(-37.03, 36.86) * mm});
            skLineSegment(sketch, "E342.MirrorCS", {"start": v(-37.03, 36.86) * mm, "end": v(-38.66, 35.23) * mm});
            skLineSegment(sketch, "E343.MirrorCS", {"start": v(-38.66, 32.88) * mm, "end": v(-38.66, 33.64) * mm});
            skLineSegment(sketch, "E344.MirrorCS", {"start": v(-37.03, 29.66) * mm, "end": v(-38.66, 31.3) * mm});
            skLineSegment(sketch, "E345.MirrorCS", {"start": v(-33.92, 29.66) * mm, "end": v(-37.03, 29.66) * mm});
            skLineSegment(sketch, "E346.MirrorCS", {"start": v(-33.92, 31.2) * mm, "end": v(-33.92, 29.66) * mm});
            skLineSegment(sketch, "E347.MirrorCS", {"start": v(-38.66, 31.3) * mm, "end": v(-38.66, 32.88) * mm});
            skLineSegment(sketch, "E348.MirrorCS", {"start": v(-38.66, 35.23) * mm, "end": v(-38.66, 33.64) * mm});
            skLineSegment(sketch, "E349", {"start": v(-31.83, 29.57) * mm, "end": v(-32.3, 29.57) * mm});
            skLineSegment(sketch, "E350", {"start": v(-31.83, 36.95) * mm, "end": v(-32.3, 36.95) * mm});
            skLineSegment(sketch, "E351", {"start": v(-54.76, 4.25) * mm, "end": v(-54.76, 12.75) * mm, "construction": true});
            skLineSegment(sketch, "E352", {"start": v(-52.9, 12.1) * mm, "end": v(-49.78, 12.1) * mm});
            skLineSegment(sketch, "E353", {"start": v(-49.78, 12.1) * mm, "end": v(-48.16, 10.47) * mm});
            skLineSegment(sketch, "E354.MirrorCS", {"start": v(-56.61, 12.1) * mm, "end": v(-59.73, 12.1) * mm});
            skLineSegment(sketch, "E355.MirrorCS", {"start": v(-59.73, 4.9) * mm, "end": v(-61.36, 6.53) * mm});
            skLineSegment(sketch, "E356", {"start": v(-52.9, 4.9) * mm, "end": v(-49.78, 4.9) * mm});
            skLineSegment(sketch, "E357.MirrorCS", {"start": v(-56.61, 4.9) * mm, "end": v(-59.73, 4.9) * mm});
            skLineSegment(sketch, "E358", {"start": v(-48.16, 8.12) * mm, "end": v(-48.16, 8.88) * mm});
            skLineSegment(sketch, "E359", {"start": v(-54.52, 12.2) * mm, "end": v(-54.99, 12.2) * mm});
            skLineSegment(sketch, "E360.MirrorCS", {"start": v(-54.99, 12.2) * mm, "end": v(-56.27, 10.9) * mm});
            skLineSegment(sketch, "E361", {"start": v(-54.52, 4.8) * mm, "end": v(-53.24, 6.1) * mm});
            skLineSegment(sketch, "E362", {"start": v(-49.78, 4.9) * mm, "end": v(-48.16, 6.53) * mm});
            skLineSegment(sketch, "E363.MirrorCS", {"start": v(-59.73, 12.1) * mm, "end": v(-61.36, 10.47) * mm});
            skLineSegment(sketch, "E364", {"start": v(-52.9, 11.04) * mm, "end": v(-52.9, 12.1) * mm});
            skLineSegment(sketch, "E365.MirrorCS", {"start": v(-61.36, 8.12) * mm, "end": v(-61.36, 8.88) * mm});
            skLineSegment(sketch, "E366", {"start": v(-54.52, 12.2) * mm, "end": v(-53.24, 10.9) * mm});
            skLineSegment(sketch, "E367", {"start": v(-48.16, 10.47) * mm, "end": v(-48.16, 8.88) * mm});
            skLineSegment(sketch, "E368", {"start": v(-48.16, 6.53) * mm, "end": v(-48.16, 8.12) * mm});
            skLineSegment(sketch, "E369.MirrorCS", {"start": v(-61.36, 6.53) * mm, "end": v(-61.36, 8.12) * mm});
            skLineSegment(sketch, "E370.MirrorCS", {"start": v(-61.36, 10.47) * mm, "end": v(-61.36, 8.88) * mm});
            skLineSegment(sketch, "E371", {"start": v(-54.52, 4.8) * mm, "end": v(-54.99, 4.8) * mm});
            skLineSegment(sketch, "E372.MirrorCS", {"start": v(-54.99, 4.8) * mm, "end": v(-56.27, 6.1) * mm});
            skArc(sketch, "E373.MirrorCS", {"start": v(-56.27, 10.9) * mm, "mid": v(-56.48, 10.86) * mm, "end": v(-56.61, 11.04) * mm});
            skLineSegment(sketch, "E374.MirrorCS", {"start": v(-56.61, 11.04) * mm, "end": v(-56.61, 12.1) * mm});
            skLineSegment(sketch, "E375.MirrorCS", {"start": v(-56.61, 5.96) * mm, "end": v(-56.61, 4.9) * mm});
            skLineSegment(sketch, "E376", {"start": v(-52.9, 5.96) * mm, "end": v(-52.9, 4.9) * mm});
            skArc(sketch, "E377", {"start": v(-53.24, 6.1) * mm, "mid": v(-53.03, 6.14) * mm, "end": v(-52.9, 5.96) * mm});
            skArc(sketch, "E378", {"start": v(-53.24, 10.9) * mm, "mid": v(-53.03, 10.86) * mm, "end": v(-52.9, 11.04) * mm});
            skArc(sketch, "E379.MirrorCS", {"start": v(-56.27, 6.1) * mm, "mid": v(-56.48, 6.14) * mm, "end": v(-56.61, 5.96) * mm});
            skLineSegment(sketch, "E380", {"start": v(-54.76, 4.8) * mm, "end": v(-54.76, 12.2) * mm});
            skLineSegment(sketch, "E381", {"start": v(-32.06, 29.57) * mm, "end": v(-32.06, 36.95) * mm, "construction": true});
            skLineSegment(sketch, "E382", {"start": v(-32.06, 33.26) * mm, "end": v(-32.06, 23.26) * mm, "construction": true});
            skLineSegment(sketch, "E383.bottom", {"start": v(-32.06, 23.26) * mm, "end": v(-12.06, 23.26) * mm, "construction": true});
            skLineSegment(sketch, "E383.top", {"start": v(-32.06, 43.26) * mm, "end": v(-12.06, 43.26) * mm, "construction": true});
            skLineSegment(sketch, "E383.left", {"start": v(-32.06, 23.26) * mm, "end": v(-32.06, 43.26) * mm, "construction": true});
            skLineSegment(sketch, "E383.right", {"start": v(-12.06, 23.26) * mm, "end": v(-12.06, 43.26) * mm, "construction": true});
            skLineSegment(sketch, "E384", {"start": v(-32.06, 23.26) * mm, "end": v(-12.06, 43.26) * mm, "construction": true});
            skCircle(sketch, "E385", {"center": v(-22.06, 33.26) * mm, "radius": 2.5 * mm});
            skLineSegment(sketch, "E386", {"start": v(-12.06, 43.26) * mm, "end": v(-32.06, 43.26) * mm});
            skLineSegment(sketch, "E387", {"start": v(-12.06, 23.26) * mm, "end": v(-12.06, 43.26) * mm});
            skLineSegment(sketch, "E388", {"start": v(-32.06, 23.26) * mm, "end": v(-12.06, 23.26) * mm});
            skLineSegment(sketch, "E389.MirrorCS", {"start": v(-32.06, 23.26) * mm, "end": v(-52.06, 23.26) * mm});
            skLineSegment(sketch, "E390.MirrorCS", {"start": v(-52.06, 23.26) * mm, "end": v(-52.06, 43.26) * mm});
            skLineSegment(sketch, "E391.MirrorCS", {"start": v(-52.06, 43.26) * mm, "end": v(-32.06, 43.26) * mm});
            skCircle(sketch, "E392.MirrorC", {"center": v(-42.06, 33.26) * mm, "radius": 2.5 * mm});
            skSolve(sketch);
        }
        {
            var Q0;
            Q0=qCreatedBy(makeId("Top.planeOp"),FACE);
            var sketch = newSketch(context, id + "F1", { "sketchPlane" : qUnion([Q0])});
            skLineSegment(sketch, "E393", {"start": v(-75.83, -59.96) * mm, "end": v(-74.54, -61.24) * mm});
            skArc(sketch, "E394", {"start": v(-74.54, -61.24) * mm, "mid": v(-74.33, -61.29) * mm, "end": v(-74.2, -61.1) * mm});
            skLineSegment(sketch, "E395", {"start": v(-74.2, -61.1) * mm, "end": v(-74.2, -60.05) * mm});
            skLineSegment(sketch, "E396", {"start": v(-74.2, -60.05) * mm, "end": v(-71.09, -60.05) * mm});
            skLineSegment(sketch, "E397", {"start": v(-71.09, -60.05) * mm, "end": v(-69.46, -61.68) * mm});
            skLineSegment(sketch, "E398", {"start": v(-69.46, -61.68) * mm, "end": v(-69.46, -63.27) * mm});
            skLineSegment(sketch, "E399", {"start": v(-69.46, -63.27) * mm, "end": v(-69.08, -63.65) * mm});
            skLineSegment(sketch, "E400", {"start": v(-69.46, -64.03) * mm, "end": v(-69.08, -63.65) * mm});
            skLineSegment(sketch, "E401", {"start": v(-69.46, -65.61) * mm, "end": v(-69.46, -64.03) * mm});
            skLineSegment(sketch, "E402", {"start": v(-71.09, -67.25) * mm, "end": v(-69.46, -65.61) * mm});
            skLineSegment(sketch, "E403", {"start": v(-74.2, -67.25) * mm, "end": v(-71.09, -67.25) * mm});
            skLineSegment(sketch, "E404", {"start": v(-74.2, -66.19) * mm, "end": v(-74.2, -67.25) * mm});
            skArc(sketch, "E405", {"start": v(-74.54, -66.06) * mm, "mid": v(-74.33, -66.01) * mm, "end": v(-74.2, -66.19) * mm});
            skLineSegment(sketch, "E406", {"start": v(-75.83, -67.34) * mm, "end": v(-74.54, -66.06) * mm});
            skArc(sketch, "E407", {"start": v(-76.06, -67.9) * mm, "mid": v(-76, -67.6) * mm, "end": v(-75.83, -67.34) * mm});
            skLineSegment(sketch, "E408", {"start": v(-76.06, -72.23) * mm, "end": v(-76.06, -67.9) * mm});
            skArc(sketch, "E409", {"start": v(-74.66, -73.65) * mm, "mid": v(-75.63, -73.2) * mm, "end": v(-76.06, -72.23) * mm});
            skLineSegment(sketch, "E410", {"start": v(-70.1, -73.65) * mm, "end": v(-74.66, -73.65) * mm});
            skArc(sketch, "E411", {"start": v(-69.53, -73.41) * mm, "mid": v(-69.8, -73.59) * mm, "end": v(-70.1, -73.65) * mm});
            skLineSegment(sketch, "E412", {"start": v(-68.43, -72.31) * mm, "end": v(-69.53, -73.41) * mm});
            skArc(sketch, "E413", {"start": v(-68.6, -71.88) * mm, "mid": v(-68.38, -72.04) * mm, "end": v(-68.43, -72.31) * mm});
            skLineSegment(sketch, "E414", {"start": v(-69.66, -71.88) * mm, "end": v(-68.6, -71.88) * mm});
            skLineSegment(sketch, "E415", {"start": v(-69.66, -68.68) * mm, "end": v(-69.66, -71.88) * mm});
            skLineSegment(sketch, "E416", {"start": v(-68.06, -67.08) * mm, "end": v(-69.66, -68.68) * mm});
            skLineSegment(sketch, "E417", {"start": v(-66.36, -67.08) * mm, "end": v(-68.06, -67.08) * mm});
            skLineSegment(sketch, "E418", {"start": v(-66.06, -66.82) * mm, "end": v(-66.36, -67.08) * mm});
            skLineSegment(sketch, "E419", {"start": v(-66.06, -66.82) * mm, "end": v(-65.76, -67.08) * mm});
            skLineSegment(sketch, "E420", {"start": v(-65.76, -67.08) * mm, "end": v(-64.05, -67.08) * mm});
            skLineSegment(sketch, "E421", {"start": v(-64.05, -67.08) * mm, "end": v(-62.46, -68.68) * mm});
            skLineSegment(sketch, "E422", {"start": v(-62.46, -68.68) * mm, "end": v(-62.46, -71.88) * mm});
            skLineSegment(sketch, "E423", {"start": v(-62.46, -71.88) * mm, "end": v(-63.5, -71.88) * mm});
            skArc(sketch, "E424", {"start": v(-63.5, -71.88) * mm, "mid": v(-63.74, -72.04) * mm, "end": v(-63.68, -72.31) * mm});
            skLineSegment(sketch, "E425", {"start": v(-63.68, -72.31) * mm, "end": v(-62.58, -73.41) * mm});
            skArc(sketch, "E426", {"start": v(-62.58, -73.41) * mm, "mid": v(-62.32, -73.59) * mm, "end": v(-62.01, -73.65) * mm});
            skLineSegment(sketch, "E427", {"start": v(-62.01, -73.65) * mm, "end": v(-57.46, -73.65) * mm});
            skArc(sketch, "E428", {"start": v(-57.46, -73.65) * mm, "mid": v(-56.49, -73.2) * mm, "end": v(-56.06, -72.23) * mm});
            skLineSegment(sketch, "E429", {"start": v(-56.06, -72.23) * mm, "end": v(-56.06, -67.9) * mm});
            skArc(sketch, "E430", {"start": v(-56.06, -67.9) * mm, "mid": v(-56.12, -67.6) * mm, "end": v(-56.29, -67.34) * mm});
            skLineSegment(sketch, "E431", {"start": v(-56.29, -67.34) * mm, "end": v(-57.57, -66.06) * mm});
            skArc(sketch, "E432", {"start": v(-57.57, -66.06) * mm, "mid": v(-57.78, -66.01) * mm, "end": v(-57.91, -66.19) * mm});
            skLineSegment(sketch, "E433", {"start": v(-57.91, -66.19) * mm, "end": v(-57.91, -67.25) * mm});
            skLineSegment(sketch, "E434", {"start": v(-57.91, -67.25) * mm, "end": v(-61.03, -67.25) * mm});
            skLineSegment(sketch, "E435", {"start": v(-61.03, -67.25) * mm, "end": v(-62.66, -65.61) * mm});
            skLineSegment(sketch, "E436", {"start": v(-62.66, -65.61) * mm, "end": v(-62.66, -64.03) * mm});
            skLineSegment(sketch, "E437", {"start": v(-62.66, -64.03) * mm, "end": v(-63.04, -63.65) * mm});
            skLineSegment(sketch, "E438", {"start": v(-62.66, -63.27) * mm, "end": v(-63.04, -63.65) * mm});
            skLineSegment(sketch, "E439", {"start": v(-62.66, -61.68) * mm, "end": v(-62.66, -63.27) * mm});
            skLineSegment(sketch, "E440", {"start": v(-61.03, -60.05) * mm, "end": v(-62.66, -61.68) * mm});
            skLineSegment(sketch, "E441", {"start": v(-57.91, -60.05) * mm, "end": v(-61.03, -60.05) * mm});
            skLineSegment(sketch, "E442", {"start": v(-57.91, -61.1) * mm, "end": v(-57.91, -60.05) * mm});
            skArc(sketch, "E443", {"start": v(-57.57, -61.24) * mm, "mid": v(-57.78, -61.29) * mm, "end": v(-57.91, -61.1) * mm});
            skLineSegment(sketch, "E444", {"start": v(-56.29, -59.96) * mm, "end": v(-57.57, -61.24) * mm});
            skArc(sketch, "E445", {"start": v(-56.06, -59.4) * mm, "mid": v(-56.12, -59.7) * mm, "end": v(-56.29, -59.96) * mm});
            skLineSegment(sketch, "E446", {"start": v(-56.06, -55.07) * mm, "end": v(-56.06, -59.4) * mm});
            skArc(sketch, "E447", {"start": v(-57.46, -53.65) * mm, "mid": v(-56.49, -54.1) * mm, "end": v(-56.06, -55.07) * mm});
            skLineSegment(sketch, "E448", {"start": v(-62.01, -53.65) * mm, "end": v(-57.46, -53.65) * mm});
            skArc(sketch, "E449", {"start": v(-62.58, -53.88) * mm, "mid": v(-62.32, -53.7) * mm, "end": v(-62.01, -53.65) * mm});
            skLineSegment(sketch, "E450", {"start": v(-63.68, -54.99) * mm, "end": v(-62.58, -53.88) * mm});
            skArc(sketch, "E451", {"start": v(-63.5, -55.41) * mm, "mid": v(-63.74, -55.26) * mm, "end": v(-63.68, -54.99) * mm});
            skLineSegment(sketch, "E452", {"start": v(-62.46, -55.41) * mm, "end": v(-63.5, -55.41) * mm});
            skLineSegment(sketch, "E453", {"start": v(-62.46, -58.61) * mm, "end": v(-62.46, -55.41) * mm});
            skLineSegment(sketch, "E454", {"start": v(-64.05, -60.21) * mm, "end": v(-62.46, -58.61) * mm});
            skLineSegment(sketch, "E455", {"start": v(-65.76, -60.21) * mm, "end": v(-64.05, -60.21) * mm});
            skLineSegment(sketch, "E456", {"start": v(-66.06, -60.47) * mm, "end": v(-65.76, -60.21) * mm});
            skLineSegment(sketch, "E457", {"start": v(-66.06, -60.47) * mm, "end": v(-66.36, -60.21) * mm});
            skLineSegment(sketch, "E458", {"start": v(-66.36, -60.21) * mm, "end": v(-68.06, -60.21) * mm});
            skLineSegment(sketch, "E459", {"start": v(-68.06, -60.21) * mm, "end": v(-69.66, -58.61) * mm});
            skLineSegment(sketch, "E460", {"start": v(-69.66, -58.61) * mm, "end": v(-69.66, -55.41) * mm});
            skLineSegment(sketch, "E461", {"start": v(-69.66, -55.41) * mm, "end": v(-68.6, -55.41) * mm});
            skArc(sketch, "E462", {"start": v(-68.6, -55.41) * mm, "mid": v(-68.38, -55.26) * mm, "end": v(-68.43, -54.99) * mm});
            skLineSegment(sketch, "E463", {"start": v(-68.43, -54.99) * mm, "end": v(-69.53, -53.88) * mm});
            skArc(sketch, "E464", {"start": v(-69.53, -53.88) * mm, "mid": v(-69.8, -53.7) * mm, "end": v(-70.1, -53.65) * mm});
            skLineSegment(sketch, "E465", {"start": v(-70.1, -53.65) * mm, "end": v(-74.66, -53.65) * mm});
            skArc(sketch, "E466", {"start": v(-74.66, -53.65) * mm, "mid": v(-75.63, -54.1) * mm, "end": v(-76.06, -55.07) * mm});
            skLineSegment(sketch, "E467", {"start": v(-76.06, -55.07) * mm, "end": v(-76.06, -59.4) * mm});
            skArc(sketch, "E468", {"start": v(-76.06, -59.4) * mm, "mid": v(-76, -59.7) * mm, "end": v(-75.83, -59.96) * mm});
            skLineSegment(sketch, "E469", {"start": v(-74.86, -69.03) * mm, "end": v(-74.86, -72.03) * mm});
            skArc(sketch, "E470", {"start": v(-74.86, -69.03) * mm, "mid": v(-74.77, -68.65) * mm, "end": v(-74.45, -68.45) * mm});
            skLineSegment(sketch, "E471", {"start": v(-71.45, -68.45) * mm, "end": v(-74.45, -68.45) * mm});
            skArc(sketch, "E472", {"start": v(-71.45, -68.45) * mm, "mid": v(-71, -68.58) * mm, "end": v(-70.86, -69.03) * mm});
            skLineSegment(sketch, "E473", {"start": v(-70.86, -72.03) * mm, "end": v(-70.86, -69.03) * mm});
            skArc(sketch, "E474", {"start": v(-70.86, -72.03) * mm, "mid": v(-71.07, -72.37) * mm, "end": v(-71.46, -72.45) * mm});
            skLineSegment(sketch, "E475", {"start": v(-74.46, -72.45) * mm, "end": v(-71.46, -72.45) * mm});
            skArc(sketch, "E476", {"start": v(-74.46, -72.45) * mm, "mid": v(-74.72, -72.3) * mm, "end": v(-74.86, -72.03) * mm});
            skLineSegment(sketch, "E477", {"start": v(-57.26, -58.27) * mm, "end": v(-57.26, -55.27) * mm});
            skArc(sketch, "E478", {"start": v(-57.26, -58.27) * mm, "mid": v(-57.34, -58.64) * mm, "end": v(-57.67, -58.85) * mm});
            skLineSegment(sketch, "E479", {"start": v(-60.67, -58.85) * mm, "end": v(-57.67, -58.85) * mm});
            skArc(sketch, "E480", {"start": v(-60.67, -58.85) * mm, "mid": v(-61.12, -58.71) * mm, "end": v(-61.26, -58.27) * mm});
            skLineSegment(sketch, "E481", {"start": v(-61.26, -55.27) * mm, "end": v(-61.26, -58.27) * mm});
            skArc(sketch, "E482", {"start": v(-61.26, -55.27) * mm, "mid": v(-61.05, -54.93) * mm, "end": v(-60.66, -54.85) * mm});
            skLineSegment(sketch, "E483", {"start": v(-57.66, -54.85) * mm, "end": v(-60.66, -54.85) * mm});
            skArc(sketch, "E484", {"start": v(-57.66, -54.85) * mm, "mid": v(-57.4, -55) * mm, "end": v(-57.26, -55.27) * mm});
            skArc(sketch, "E485", {"start": v(-60.67, -68.45) * mm, "mid": v(-61.12, -68.58) * mm, "end": v(-61.26, -69.03) * mm});
            skLineSegment(sketch, "E486", {"start": v(-60.67, -68.45) * mm, "end": v(-57.67, -68.45) * mm});
            skArc(sketch, "E487", {"start": v(-57.26, -69.03) * mm, "mid": v(-57.34, -68.65) * mm, "end": v(-57.67, -68.45) * mm});
            skLineSegment(sketch, "E488", {"start": v(-57.26, -69.03) * mm, "end": v(-57.26, -72.03) * mm});
            skArc(sketch, "E489", {"start": v(-57.66, -72.45) * mm, "mid": v(-57.4, -72.3) * mm, "end": v(-57.26, -72.03) * mm});
            skLineSegment(sketch, "E490", {"start": v(-57.66, -72.45) * mm, "end": v(-60.66, -72.45) * mm});
            skArc(sketch, "E491", {"start": v(-61.26, -72.03) * mm, "mid": v(-61.05, -72.37) * mm, "end": v(-60.66, -72.45) * mm});
            skLineSegment(sketch, "E492", {"start": v(-61.26, -72.03) * mm, "end": v(-61.26, -69.03) * mm});
            skCircle(sketch, "E493", {"center": v(-66.06, -63.65) * mm, "radius": 2.1 * mm});
            skArc(sketch, "E494", {"start": v(-71.45, -58.85) * mm, "mid": v(-71, -58.71) * mm, "end": v(-70.86, -58.27) * mm});
            skLineSegment(sketch, "E495", {"start": v(-71.45, -58.85) * mm, "end": v(-74.45, -58.85) * mm});
            skArc(sketch, "E496", {"start": v(-74.86, -58.27) * mm, "mid": v(-74.77, -58.64) * mm, "end": v(-74.45, -58.85) * mm});
            skLineSegment(sketch, "E497", {"start": v(-74.86, -58.27) * mm, "end": v(-74.86, -55.27) * mm});
            skArc(sketch, "E498", {"start": v(-74.46, -54.85) * mm, "mid": v(-74.72, -55) * mm, "end": v(-74.86, -55.27) * mm});
            skLineSegment(sketch, "E499", {"start": v(-74.46, -54.85) * mm, "end": v(-71.46, -54.85) * mm});
            skArc(sketch, "E500", {"start": v(-70.86, -55.27) * mm, "mid": v(-71.07, -54.93) * mm, "end": v(-71.46, -54.85) * mm});
            skLineSegment(sketch, "E501", {"start": v(-70.86, -55.27) * mm, "end": v(-70.86, -58.27) * mm});
            skSolve(sketch);
        }
        {
            var Q0;
            Q0=makeQuery(id+"F1.imprint","IMPRINT",FACE,{"disambiguationData":[TD([[makeQuery(id+"F1.imprint","IMPRINT",EDGE,{"derivedFrom":sQuery(id+"F1.wireOp",EDGE,"E393")}),1.0]])]});
            extrude(context, id + "F2", {"entities" : qUnion([Q0]), "depth" : 340 * mm});
        }
        {
            var Q0;
            Q0=qCreatedBy(makeId("Top.planeOp"),FACE);
            var sketch = newSketch(context, id + "F3", { "sketchPlane" : qUnion([Q0])});
            skCircle(sketch, "E502.cCircle", {"center": v(146.52, 92.14) * mm, "radius": 6 * mm, "construction": true});
            skLineSegment(sketch, "E502.0", {"start": v(153.43, 92.54) * mm, "end": v(150.32, 86.35) * mm});
            skLineSegment(sketch, "E502.1", {"start": v(150.32, 86.35) * mm, "end": v(143.4, 85.95) * mm});
            skLineSegment(sketch, "E502.2", {"start": v(143.4, 85.95) * mm, "end": v(139.6, 91.73) * mm});
            skLineSegment(sketch, "E502.3", {"start": v(139.6, 91.73) * mm, "end": v(142.7, 97.93) * mm});
            skLineSegment(sketch, "E502.4", {"start": v(142.7, 97.93) * mm, "end": v(149.62, 98.33) * mm});
            skLineSegment(sketch, "E502.5", {"start": v(149.62, 98.33) * mm, "end": v(153.43, 92.54) * mm});
            skPoint(sketch, "E502.0.midPoint", {"position": v(151.88, 89.45) * mm});
            skCircle(sketch, "E503", {"center": v(146.52, 92.14) * mm, "radius": 3 * mm});
            skSolve(sketch);
        }
        {
            var Q0;
            Q0=makeQuery(id+"F3.imprint","IMPRINT",FACE,{"disambiguationData":[TD([[makeQuery(id+"F3.imprint","IMPRINT",EDGE,{"derivedFrom":sQuery(id+"F3.wireOp",EDGE,"E503")}),1.0]])]});
            extrude(context, id + "F4", {"entities" : qUnion([Q0]), "depth" : 34 * mm});
        }
        {
            var Q0;
            Q0=makeQuery(id+"F3.imprint","IMPRINT",FACE,{"disambiguationData":[TD([[makeQuery(id+"F3.imprint","IMPRINT",EDGE,{"derivedFrom":sQuery(id+"F3.wireOp",EDGE,"E502.0")}),-1.0]])]});
            extrude(context, id + "F5", {"entities" : qUnion([Q0]), "operationType" : NewBodyOperationType.ADD, "depth" : 4 * mm});
        }
        {
            var Q0;
            Q0=qCreatedBy(makeId("Top.planeOp"),FACE);
            var sketch = newSketch(context, id + "F6", { "sketchPlane" : qUnion([Q0])});
            skCircle(sketch, "E504", {"center": v(66.51, 54.73) * mm, "radius": 3 * mm});
            skCircle(sketch, "E505", {"center": v(66.51, 54.73) * mm, "radius": 2 * mm});
            skSolve(sketch);
        }
        {
            var Q0;
            Q0=makeQuery(id+"F6.imprint","IMPRINT",FACE,{"disambiguationData":[TD([[makeQuery(id+"F6.imprint","IMPRINT",EDGE,{"derivedFrom":sQuery(id+"F6.wireOp",EDGE,"E504")}),1.0]])]});
            extrude(context, id + "F7", {"entities" : qUnion([Q0]), "depth" : 26 * mm});
        }
        {
            var Q0;
            Q0=qCreatedBy(makeId("Top.planeOp"),FACE);
            var sketch = newSketch(context, id + "F8", { "sketchPlane" : qUnion([Q0])});
            skCircle(sketch, "E506.cCircle", {"center": v(133.4, 42.3) * mm, "radius": 4 * mm, "construction": true});
            skLineSegment(sketch, "E506.0", {"start": v(138.01, 42.56) * mm, "end": v(135.94, 38.43) * mm});
            skLineSegment(sketch, "E506.1", {"start": v(135.94, 38.43) * mm, "end": v(131.33, 38.16) * mm});
            skLineSegment(sketch, "E506.2", {"start": v(131.33, 38.16) * mm, "end": v(128.8, 42.02) * mm});
            skLineSegment(sketch, "E506.3", {"start": v(128.8, 42.02) * mm, "end": v(130.86, 46.15) * mm});
            skLineSegment(sketch, "E506.4", {"start": v(130.86, 46.15) * mm, "end": v(135.47, 46.42) * mm});
            skLineSegment(sketch, "E506.5", {"start": v(135.47, 46.42) * mm, "end": v(138.01, 42.56) * mm});
            skPoint(sketch, "E506.0.midPoint", {"position": v(136.98, 40.5) * mm});
            skCircle(sketch, "E507", {"center": v(133.4, 42.3) * mm, "radius": 2 * mm});
            skCircle(sketch, "E508.cCircle", {"center": v(137.38, 58.52) * mm, "radius": 3.5 * mm, "construction": true});
            skLineSegment(sketch, "E508.0", {"start": v(138.97, 62.24) * mm, "end": v(141.39, 59) * mm});
            skLineSegment(sketch, "E508.1", {"start": v(141.39, 59) * mm, "end": v(139.8, 55.29) * mm});
            skLineSegment(sketch, "E508.2", {"start": v(139.8, 55.29) * mm, "end": v(135.78, 54.8) * mm});
            skLineSegment(sketch, "E508.3", {"start": v(135.78, 54.8) * mm, "end": v(133.36, 58.04) * mm});
            skLineSegment(sketch, "E508.4", {"start": v(133.36, 58.04) * mm, "end": v(134.96, 61.76) * mm});
            skLineSegment(sketch, "E508.5", {"start": v(134.96, 61.76) * mm, "end": v(138.97, 62.24) * mm});
            skPoint(sketch, "E508.0.midPoint", {"position": v(140.18, 60.62) * mm});
            skCircle(sketch, "E509", {"center": v(137.38, 58.52) * mm, "radius": 2 * mm});
            skCircle(sketch, "E510.cCircle", {"center": v(150.97, 48.26) * mm, "radius": 2.5 * mm, "construction": true});
            skLineSegment(sketch, "E510.0", {"start": v(153.83, 48.64) * mm, "end": v(152.73, 45.97) * mm});
            skLineSegment(sketch, "E510.1", {"start": v(152.73, 45.97) * mm, "end": v(149.86, 45.6) * mm});
            skLineSegment(sketch, "E510.2", {"start": v(149.86, 45.6) * mm, "end": v(148.1, 47.89) * mm});
            skLineSegment(sketch, "E510.3", {"start": v(148.1, 47.89) * mm, "end": v(149.21, 50.55) * mm});
            skLineSegment(sketch, "E510.4", {"start": v(149.21, 50.55) * mm, "end": v(152.07, 50.93) * mm});
            skLineSegment(sketch, "E510.5", {"start": v(152.07, 50.93) * mm, "end": v(153.83, 48.64) * mm});
            skPoint(sketch, "E510.0.midPoint", {"position": v(153.28, 47.3) * mm});
            skCircle(sketch, "E511", {"center": v(150.97, 48.26) * mm, "radius": 1.5 * mm});
            skSolve(sketch);
        }
        {
            var Q0;
            Q0=makeQuery(id+"F8.imprint","IMPRINT",FACE,{"disambiguationData":[TD([[makeQuery(id+"F8.imprint","IMPRINT",EDGE,{"derivedFrom":sQuery(id+"F8.wireOp",EDGE,"E506.0")}),-1.0]])]});
            extrude(context, id + "F9", {"entities" : qUnion([Q0]), "depth" : 3 * mm});
        }
        {
            var Q0;
            Q0=makeQuery(id+"F8.imprint","IMPRINT",FACE,{"disambiguationData":[TD([[makeQuery(id+"F8.imprint","IMPRINT",EDGE,{"derivedFrom":sQuery(id+"F8.wireOp",EDGE,"E507")}),1.0]])]});
            extrude(context, id + "F10", {"entities" : qUnion([Q0]), "operationType" : NewBodyOperationType.ADD, "depth" : 11 * mm});
        }
        {
            var Q0;
            Q0=qCreatedBy(makeId("Top.planeOp"),FACE);
            var sketch = newSketch(context, id + "F11", { "sketchPlane" : qUnion([Q0])});
            skCircle(sketch, "E512", {"center": v(161.7, 0) * mm, "radius": 4 * mm});
            skCircle(sketch, "E513", {"center": v(161.7, 0) * mm, "radius": 9.5 * mm});
            skCircle(sketch, "E514", {"center": v(161.7, 0) * mm, "radius": 2.5 * mm});
            skLineSegment(sketch, "E515", {"start": v(161.7, 0) * mm, "end": v(152.2, 0) * mm});
            skLineSegment(sketch, "E516", {"start": v(161.7, 0) * mm, "end": v(171.2, 0) * mm});
            skSolve(sketch);
        }
        {
            var Q0;
            Q0=makeQuery(id+"F11.imprint","IMPRINT",FACE,{"disambiguationData":[TD([[makeQuery(id+"F11.imprint","IMPRINT",EDGE,{"derivedFrom":sQuery(id+"F11.wireOp",EDGE,"E512")}),1.0]])]});
            var Q1;
            Q1=makeQuery(id+"F11.imprint","IMPRINT",FACE,{"disambiguationData":[TD([[makeQuery(id+"F11.imprint","IMPRINT",EDGE,{"derivedFrom":sQuery(id+"F11.wireOp",EDGE,"E514")}),1.0]])]});
            var Q2;
            Q2=makeQuery(id+"F11.imprint","IMPRINT",FACE,{"disambiguationData":[TD([[makeQuery(id+"F11.imprint","IMPRINT",EDGE,{"derivedFrom":sQuery(id+"F11.wireOp",EDGE,"E512")}),-1.0]])]});
            extrude(context, id + "F12", {"entities" : qUnion([Q0, Q1, Q2]), "depth" : 25 * mm});
        }
        {
            var Q0;
            Q0=makeQuery(id+"F11.imprint","IMPRINT",FACE,{"disambiguationData":[TD([[makeQuery(id+"F11.imprint","IMPRINT",EDGE,{"derivedFrom":sQuery(id+"F11.wireOp",EDGE,"E514")}),1.0]])]});
            extrude(context, id + "F13", {"entities" : qUnion([Q0]), "operationType" : NewBodyOperationType.REMOVE, "depth" : 25 * mm});
        }
        {
            var Q0;
            Q0=makeQuery(id+"F11.imprint","IMPRINT",FACE,{"disambiguationData":[TD([[makeQuery(id+"F11.imprint","IMPRINT",EDGE,{"derivedFrom":sQuery(id+"F11.wireOp",EDGE,"E512")}),1.0]])]});
            extrude(context, id + "F14", {"entities" : qUnion([Q0]), "operationType" : NewBodyOperationType.REMOVE, "depth" : 10.05 * mm});
        }
        {
            var Q0;
            {var subQ1=sQuery(id+"F11.wireOp",EDGE,"E512");var subQ5=sQuery(id+"F11.wireOp",EDGE,"E515");var subQ6=makeQuery(id+"F11.imprint","INTERSECT",VERTEX,{"derivedFrom":[subQ1,subQ5]});Q0=makeQuery(id+"F11.imprint","IMPRINT",FACE,{"disambiguationData":[TD([[makeQuery(id+"F11.imprint","IMPRINT",EDGE,{"disambiguationData":[TD([[subQ6,1.0]])],"derivedFrom":subQ1}),-1.0]])]});}
            extrude(context, id + "F15", {"entities" : qUnion([Q0]), "operationType" : NewBodyOperationType.REMOVE, "depth" : 12.82 * mm, "hasSecondDirection" : true, "secondDirectionOppositeDirection" : false, "secondDirectionDepth" : 11.8 * mm});
        }
        {
            var Q0;
            {var subQ0=sQuery(id+"F11.wireOp",EDGE,"E515");var subQ1=sQuery(id+"F11.wireOp",EDGE,"E512");var subQ2=makeQuery(id+"F11.imprint","INTERSECT",VERTEX,{"derivedFrom":[subQ1,subQ0]});Q0=makeQuery(id+"F11.imprint","IMPRINT",FACE,{"disambiguationData":[TD([[makeQuery(id+"F11.imprint","IMPRINT",EDGE,{"disambiguationData":[TD([[subQ2,-1.0]])],"derivedFrom":subQ1}),-1.0]])]});}
            extrude(context, id + "F16", {"entities" : qUnion([Q0]), "operationType" : NewBodyOperationType.REMOVE, "depth" : 14.2 * mm, "hasSecondDirection" : true, "secondDirectionOppositeDirection" : false, "secondDirectionDepth" : 13.18 * mm});
        }
        {
            var Q0;
            {var subQ1=sQuery(id+"F11.wireOp",EDGE,"E512");var subQ5=sQuery(id+"F11.wireOp",EDGE,"E515");var subQ6=makeQuery(id+"F11.imprint","INTERSECT",VERTEX,{"derivedFrom":[subQ1,subQ5]});Q0=makeQuery(id+"F11.imprint","IMPRINT",FACE,{"disambiguationData":[TD([[makeQuery(id+"F11.imprint","IMPRINT",EDGE,{"disambiguationData":[TD([[subQ6,1.0]])],"derivedFrom":subQ1}),-1.0]])]});}
            extrude(context, id + "F17", {"entities" : qUnion([Q0]), "operationType" : NewBodyOperationType.REMOVE, "depth" : 16.02 * mm, "hasSecondDirection" : true, "secondDirectionOppositeDirection" : false, "secondDirectionDepth" : 14.75 * mm});
        }
        {
            var Q0;
            {var subQ0=sQuery(id+"F11.wireOp",EDGE,"E515");var subQ1=sQuery(id+"F11.wireOp",EDGE,"E512");var subQ2=makeQuery(id+"F11.imprint","INTERSECT",VERTEX,{"derivedFrom":[subQ1,subQ0]});Q0=makeQuery(id+"F11.imprint","IMPRINT",FACE,{"disambiguationData":[TD([[makeQuery(id+"F11.imprint","IMPRINT",EDGE,{"disambiguationData":[TD([[subQ2,-1.0]])],"derivedFrom":subQ1}),-1.0]])]});}
            extrude(context, id + "F18", {"entities" : qUnion([Q0]), "operationType" : NewBodyOperationType.REMOVE, "depth" : 11.6 * mm, "hasSecondDirection" : true, "secondDirectionOppositeDirection" : false, "secondDirectionDepth" : 10.6 * mm});
        }
        {
            var Q0;
            Q0=qCreatedBy(makeId("Top.planeOp"),FACE);
            var sketch = newSketch(context, id + "F19", { "sketchPlane" : qUnion([Q0])});
            skCircle(sketch, "E517", {"center": v(83.7, -20.1) * mm, "radius": 5 * mm});
            skCircle(sketch, "E518", {"center": v(83.7, -20.1) * mm, "radius": 4.5 * mm});
            skCircle(sketch, "E519", {"center": v(83.7, -20.1) * mm, "radius": 4 * mm});
            skCircle(sketch, "E520", {"center": v(83.7, -20.1) * mm, "radius": 3 * mm});
            skCircle(sketch, "E521", {"center": v(85.15, -36.9) * mm, "radius": 3.75 * mm});
            skCircle(sketch, "E522", {"center": v(85.15, -36.9) * mm, "radius": 9 * mm});
            skCircle(sketch, "E523", {"center": v(85.15, -36.9) * mm, "radius": 6.5 * mm});
            skCircle(sketch, "E524", {"center": v(85.15, -36.9) * mm, "radius": 3.05 * mm});
            skSolve(sketch);
        }
        {
            var Q0;
            Q0=makeQuery(id+"F0.imprint","IMPRINT",FACE,{"disambiguationData":[TD([[makeQuery(id+"F0.imprint","IMPRINT",EDGE,{"derivedFrom":sQuery(id+"F0.wireOp",EDGE,"E218")}),1.0]])]});
            extrude(context, id + "F20", {"entities" : qUnion([Q0]), "operationType" : NewBodyOperationType.ADD, "depth" : 200 * mm});
        }
        {
            var Q0;
            Q0=qCreatedBy(makeId("Top.planeOp"),FACE);
            var sketch = newSketch(context, id + "F21", { "sketchPlane" : qUnion([Q0])});
            skCircle(sketch, "E525", {"center": v(-212.21, -129.41) * mm, "radius": 2.5 * mm});
            skCircle(sketch, "E526.cCircle", {"center": v(-195.56, -130.6) * mm, "radius": 4.4 * mm, "construction": true});
            skLineSegment(sketch, "E526.0", {"start": v(-195.56, -126.21) * mm, "end": v(-191.76, -128.4) * mm});
            skLineSegment(sketch, "E526.1", {"start": v(-191.76, -128.4) * mm, "end": v(-191.76, -132.8) * mm});
            skLineSegment(sketch, "E526.2", {"start": v(-191.76, -132.8) * mm, "end": v(-195.56, -135) * mm});
            skLineSegment(sketch, "E526.3", {"start": v(-195.56, -135) * mm, "end": v(-199.37, -132.8) * mm});
            skLineSegment(sketch, "E526.4", {"start": v(-199.37, -132.8) * mm, "end": v(-199.37, -128.4) * mm});
            skLineSegment(sketch, "E526.5", {"start": v(-199.37, -128.4) * mm, "end": v(-195.56, -126.21) * mm});
            skCircle(sketch, "E527", {"center": v(-195.56, -130.6) * mm, "radius": 2.5 * mm});
            skSolve(sketch);
        }
        {
            var Q0;
            Q0=makeQuery(id+"F21.imprint","IMPRINT",FACE,{"disambiguationData":[TD([[makeQuery(id+"F21.imprint","IMPRINT",EDGE,{"derivedFrom":sQuery(id+"F21.wireOp",EDGE,"E525")}),1.0]])]});
            extrude(context, id + "F22", {"entities" : qUnion([Q0]), "depth" : 210 * mm});
        }
        {
            var Q0;
            Q0=makeQuery(id+"F21.imprint","IMPRINT",FACE,{"disambiguationData":[TD([[makeQuery(id+"F21.imprint","IMPRINT",EDGE,{"derivedFrom":sQuery(id+"F21.wireOp",EDGE,"E526.0")}),-1.0]])]});
            extrude(context, id + "F23", {"entities" : qUnion([Q0]), "depth" : 20 * mm});
        }
        {
            var Q0;
            Q0=qCreatedBy(makeId("Top.planeOp"),FACE);
            var sketch = newSketch(context, id + "F24", { "sketchPlane" : qUnion([Q0])});
            skLineSegment(sketch, "E528.bottom", {"start": v(78.88, -135.44) * mm, "end": v(97.38, -135.44) * mm});
            skLineSegment(sketch, "E528.top", {"start": v(78.88, -155.44) * mm, "end": v(97.38, -155.44) * mm});
            skLineSegment(sketch, "E528.left", {"start": v(78.88, -135.44) * mm, "end": v(78.88, -155.44) * mm});
            skLineSegment(sketch, "E528.right", {"start": v(97.38, -135.44) * mm, "end": v(97.38, -155.44) * mm});
            skCircle(sketch, "E529", {"center": v(83.47, -145.44) * mm, "radius": 2 * mm});
            skLineSegment(sketch, "E530", {"start": v(88.13, -145.44) * mm, "end": v(88.13, -135.44) * mm, "construction": true});
            skCircle(sketch, "E531.MirrorC", {"center": v(92.79, -145.44) * mm, "radius": 2 * mm});
            skLineSegment(sketch, "E532", {"start": v(83.52, -143.44) * mm, "end": v(92.79, -143.44) * mm});
            skLineSegment(sketch, "E533", {"start": v(92.79, -147.44) * mm, "end": v(83.47, -147.44) * mm});
            skSolve(sketch);
        }
        {
            var Q0;
            Q0=makeQuery(id+"F24.imprint","IMPRINT",FACE,{"disambiguationData":[TD([[makeQuery(id+"F24.imprint","IMPRINT",EDGE,{"derivedFrom":sQuery(id+"F24.wireOp",EDGE,"E528.bottom")}),-1.0]])]});
            extrude(context, id + "F25", {"entities" : qUnion([Q0]), "depth" : 2 * mm});
        }
        {
            var Q0;
            Q0=makeQuery(id+"F25.opExtrude","SWEPT_FACE",FACE,{"disambiguationData":[OSD([sQuery(id+"F24.wireOp",EDGE,"E528.right")])]});
            var sketch = newSketch(context, id + "F26", { "sketchPlane" : qUnion([Q0])});
            skLineSegment(sketch, "E534.bottom", {"start": v(-155.44, 0) * mm, "end": v(-135.44, 0) * mm});
            skLineSegment(sketch, "E534.top", {"start": v(-155.44, 20) * mm, "end": v(-135.44, 20) * mm});
            skLineSegment(sketch, "E534.left", {"start": v(-155.44, 0) * mm, "end": v(-155.44, 20) * mm});
            skLineSegment(sketch, "E534.right", {"start": v(-135.44, 0) * mm, "end": v(-135.44, 20) * mm});
            skLineSegment(sketch, "E535", {"start": v(-145.44, 20) * mm, "end": v(-145.44, 0) * mm, "construction": true});
            skCircle(sketch, "E536", {"center": v(-145.44, 15.23) * mm, "radius": 2 * mm});
            skCircle(sketch, "E537", {"center": v(-145.44, 7) * mm, "radius": 2 * mm});
            skLineSegment(sketch, "E538", {"start": v(-147.44, 7) * mm, "end": v(-147.44, 15.23) * mm});
            skLineSegment(sketch, "E539", {"start": v(-147.44, 15.23) * mm, "end": v(-143.44, 15.23) * mm});
            skLineSegment(sketch, "E540", {"start": v(-143.44, 15.23) * mm, "end": v(-143.44, 7) * mm});
            skSolve(sketch);
        }
        {
            var Q0;
            {var subQ6=sQuery(id+"F26.wireOp",EDGE,"E534.top");Q0=makeQuery(id+"F26.imprint","IMPRINT",FACE,{"disambiguationData":[TD([[makeQuery(id+"F26.imprint","IMPRINT",EDGE,{"derivedFrom":subQ6}),-1.0]])]});}
            var Q1;
            {var subQ0=sQuery(id+"F26.wireOp",EDGE,"E534.bottom");Q1=makeQuery(id+"F26.imprint","IMPRINT",FACE,{"disambiguationData":[TD([[makeQuery(id+"F26.imprint","IMPRINT",EDGE,{"derivedFrom":subQ0}),-1.0]])]});}
            extrude(context, id + "F27", {"entities" : qUnion([Q0, Q1]), "operationType" : NewBodyOperationType.ADD, "depth" : 1.5 * mm});
        }
        {
            var Q0;
            Q0=makeQuery(id+"FSQLS7P4pgP4EKH_10.boolean.opBoolean","MERGE",FACE,{"derivedFrom":[makeQuery(id+"F27.boolean.opBoolean","MERGE",FACE,{"derivedFrom":[makeQuery(id+"F25.opExtrude","SWEPT_FACE",FACE,{"disambiguationData":[OSD([sQuery(id+"F24.wireOp",EDGE,"E528.top")])]}),makeQuery(id+"F27.opExtrude","SWEPT_FACE",FACE,{"disambiguationData":[OSD([sQuery(id+"F26.wireOp",EDGE,"E534.left")])]})]}),makeQuery(id+"FSQLS7P4pgP4EKH_10.opExtrude","CAP_FACE",FACE,{"disambiguationData":[OSD([sQuery(id+"FQXSqbNVooji3jg_10.wireOp",EDGE,"c593874d-de25-46d5-b0ce-f0ffeecd6899"),sQuery(id+"FQXSqbNVooji3jg_10.wireOp",EDGE,"34f790f1-ddf9-4c0c-bca9-d7dcb48ef748"),sQuery(id+"FQXSqbNVooji3jg_10.wireOp",EDGE,"8fd43067-58ef-4969-ac75-a588e6ec1421")])],"isStart":true})]});
            extrude(context, id + "F28", {"entities" : qUnion([Q0]), "operationType" : NewBodyOperationType.ADD, "oppositeDirection" : true, "depth" : 20 * mm, "hasSecondDirection" : true, "secondDirectionOppositeDirection" : true, "secondDirectionDepth" : 18.5 * mm});
        }
        {
            var Q0;
            Q0=makeQuery(id+"F19.imprint","IMPRINT",FACE,{"disambiguationData":[TD([[makeQuery(id+"F19.imprint","IMPRINT",EDGE,{"derivedFrom":sQuery(id+"F19.wireOp",EDGE,"E519")}),1.0]])]});
            var Q1;
            Q1=makeQuery(id+"F19.imprint","IMPRINT",FACE,{"disambiguationData":[TD([[makeQuery(id+"F19.imprint","IMPRINT",EDGE,{"derivedFrom":sQuery(id+"F19.wireOp",EDGE,"E517")}),1.0]])]});
            extrude(context, id + "F29", {"entities" : qUnion([Q0, Q1]), "operationType" : NewBodyOperationType.ADD, "depth" : 3 * mm});
        }
        {
            var Q0;
            Q0=makeQuery(id+"F19.imprint","IMPRINT",FACE,{"disambiguationData":[TD([[makeQuery(id+"F19.imprint","IMPRINT",EDGE,{"derivedFrom":sQuery(id+"F19.wireOp",EDGE,"E518")}),1.0]])]});
            extrude(context, id + "F30", {"entities" : qUnion([Q0]), "operationType" : NewBodyOperationType.ADD, "depth" : 2.8 * mm});
        }
        {
            var Q0;
            Q0=makeQuery(id+"F30.opExtrude","CAP_FACE",FACE,{"disambiguationData":[OSD([sQuery(id+"F19.wireOp",EDGE,"E518"),sQuery(id+"F19.wireOp",EDGE,"E519")])],"isStart":true});
            extrude(context, id + "F31", {"entities" : qUnion([Q0]), "operationType" : NewBodyOperationType.REMOVE, "oppositeDirection" : true, "depth" : 0.2 * mm});
        }
        {
            var Q0;
            Q0=makeQuery(id+"F19.imprint","IMPRINT",FACE,{"disambiguationData":[TD([[makeQuery(id+"F19.imprint","IMPRINT",EDGE,{"derivedFrom":sQuery(id+"F19.wireOp",EDGE,"E521")}),1.0]])]});
            extrude(context, id + "F32", {"entities" : qUnion([Q0]), "operationType" : NewBodyOperationType.ADD, "depth" : 1.5 * mm});
        }
        {
            var Q0;
            Q0=makeQuery(id+"F19.imprint","IMPRINT",FACE,{"disambiguationData":[TD([[makeQuery(id+"F19.imprint","IMPRINT",EDGE,{"derivedFrom":sQuery(id+"F19.wireOp",EDGE,"E521")}),-1.0]])]});
            var Q1;
            Q1=makeQuery(id+"F19.imprint","IMPRINT",FACE,{"disambiguationData":[TD([[makeQuery(id+"F19.imprint","IMPRINT",EDGE,{"derivedFrom":sQuery(id+"F19.wireOp",EDGE,"E522")}),1.0]])]});
            extrude(context, id + "F33", {"entities" : qUnion([Q0, Q1]), "operationType" : NewBodyOperationType.ADD, "depth" : 0.8 * mm});
        }
        {
            var Q0;
            Q0=makeQuery(id+"F27.boolean.opBoolean","MERGE",FACE,{"derivedFrom":[makeQuery(id+"F25.opExtrude","SWEPT_FACE",FACE,{"disambiguationData":[OSD([sQuery(id+"F24.wireOp",EDGE,"E528.top")])]}),makeQuery(id+"F27.opExtrude","SWEPT_FACE",FACE,{"disambiguationData":[OSD([sQuery(id+"F26.wireOp",EDGE,"E534.left")])]})]});
            var sketch = newSketch(context, id + "F34", { "sketchPlane" : qUnion([Q0])});
            skLineSegment(sketch, "E541", {"start": v(78.88, 2) * mm, "end": v(97.38, 20) * mm});
            skLineSegment(sketch, "E542", {"start": v(97.38, 20) * mm, "end": v(97.38, 2) * mm});
            skLineSegment(sketch, "E543", {"start": v(97.38, 2) * mm, "end": v(78.88, 2) * mm});
            skSolve(sketch);
        }
        {
            var Q0;
            Q0=makeQuery(id+"F34.imprint","IMPRINT",FACE,{"disambiguationData":[TD([[makeQuery(id+"F34.imprint","IMPRINT",EDGE,{"derivedFrom":sQuery(id+"F34.wireOp",EDGE,"E541")}),-1.0]])]});
            extrude(context, id + "F35", {"entities" : qUnion([Q0]), "operationType" : NewBodyOperationType.ADD, "oppositeDirection" : true, "depth" : 2 * mm});
        }
        {
            var Q0;
            Q0=makeQuery(id+"F27.boolean.opBoolean","MERGE",FACE,{"derivedFrom":[makeQuery(id+"F25.opExtrude","SWEPT_FACE",FACE,{"disambiguationData":[OSD([sQuery(id+"F24.wireOp",EDGE,"E528.bottom")])]}),makeQuery(id+"F27.opExtrude","SWEPT_FACE",FACE,{"disambiguationData":[OSD([sQuery(id+"F26.wireOp",EDGE,"E534.right")])]})]});
            var sketch = newSketch(context, id + "F36", { "sketchPlane" : qUnion([Q0])});
            skLineSegment(sketch, "E544", {"start": v(-97.38, 20) * mm, "end": v(-78.88, 2) * mm});
            skSolve(sketch);
        }
        {
            var Q0;
            Q0=makeQuery(id+"F36.imprint","IMPRINT",FACE,{"disambiguationData":[TD([[makeQuery(id+"F36.imprint","IMPRINT",EDGE,{"derivedFrom":sQuery(id+"F36.wireOp",EDGE,"E544")}),-1.0]])]});
            extrude(context, id + "F37", {"entities" : qUnion([Q0]), "operationType" : NewBodyOperationType.ADD, "oppositeDirection" : true, "depth" : 2 * mm});
        }
        {
            var Q0;
            Q0=makeQuery(id+"F8.imprint","IMPRINT",FACE,{"disambiguationData":[TD([[makeQuery(id+"F8.imprint","IMPRINT",EDGE,{"derivedFrom":sQuery(id+"F8.wireOp",EDGE,"E506.0")}),-1.0]])]});
            extrude(context, id + "F38", {"entities" : qUnion([Q0]), "oppositeDirection" : true, "depth" : 3 * mm});
        }
        {
            var Q0;
            Q0=makeQuery(id+"F8.imprint","IMPRINT",FACE,{"disambiguationData":[TD([[makeQuery(id+"F8.imprint","IMPRINT",EDGE,{"derivedFrom":sQuery(id+"F8.wireOp",EDGE,"E507")}),1.0]])]});
            extrude(context, id + "F39", {"entities" : qUnion([Q0]), "oppositeDirection" : true, "depth" : 15 * mm});
        }
        {
            var Q0;
            Q0=makeQuery(id+"F8.imprint","IMPRINT",FACE,{"disambiguationData":[TD([[makeQuery(id+"F8.imprint","IMPRINT",EDGE,{"derivedFrom":sQuery(id+"F8.wireOp",EDGE,"E508.0")}),-1.0]])]});
            extrude(context, id + "F40", {"entities" : qUnion([Q0]), "depth" : 3 * mm});
        }
        {
            var Q0;
            Q0=makeQuery(id+"F40.opExtrude","CAP_EDGE",EDGE,{"disambiguationData":[OSD([sQuery(id+"F8.wireOp",EDGE,"E508.1")])],"isStart":false});
            var Q1;
            Q1=makeQuery(id+"F40.opExtrude","CAP_EDGE",EDGE,{"disambiguationData":[OSD([sQuery(id+"F8.wireOp",EDGE,"E508.3")])],"isStart":false});
            var Q2;
            Q2=makeQuery(id+"F40.opExtrude","CAP_EDGE",EDGE,{"disambiguationData":[OSD([sQuery(id+"F8.wireOp",EDGE,"E508.4")])],"isStart":false});
            var Q3;
            Q3=makeQuery(id+"F40.opExtrude","CAP_EDGE",EDGE,{"disambiguationData":[OSD([sQuery(id+"F8.wireOp",EDGE,"E508.5")])],"isStart":false});
            var Q4;
            Q4=makeQuery(id+"F40.opExtrude","CAP_EDGE",EDGE,{"disambiguationData":[OSD([sQuery(id+"F8.wireOp",EDGE,"E508.0")])],"isStart":false});
            var Q5;
            Q5=makeQuery(id+"F40.opExtrude","CAP_EDGE",EDGE,{"disambiguationData":[OSD([sQuery(id+"F8.wireOp",EDGE,"E508.2")])],"isStart":false});
            var Q6;
            Q6=makeQuery(id+"F40.opExtrude","CAP_FACE",FACE,{"disambiguationData":[OSD([sQuery(id+"F8.wireOp",EDGE,"E508.0"),sQuery(id+"F8.wireOp",EDGE,"E508.1"),sQuery(id+"F8.wireOp",EDGE,"E508.2"),sQuery(id+"F8.wireOp",EDGE,"E508.3"),sQuery(id+"F8.wireOp",EDGE,"E508.4"),sQuery(id+"F8.wireOp",EDGE,"E508.5"),sQuery(id+"F8.wireOp",EDGE,"E509")])],"isStart":true});
            fillet(context, id + "F41", {"entities" : qUnion([Q0, Q1, Q2, Q3, Q4, Q5, Q6]), "radius" : 0.5 * mm, "tangentPropagation" : true, "allowEdgeOverflow" : false});
        }
        {
            var Q0;
            Q0=makeQuery(id+"F8.imprint","IMPRINT",FACE,{"disambiguationData":[TD([[makeQuery(id+"F8.imprint","IMPRINT",EDGE,{"derivedFrom":sQuery(id+"F8.wireOp",EDGE,"E510.0")}),-1.0]])]});
            var Q1;
            Q1=makeQuery(id+"F8.imprint","IMPRINT",FACE,{"disambiguationData":[TD([[makeQuery(id+"F8.imprint","IMPRINT",EDGE,{"derivedFrom":sQuery(id+"F8.wireOp",EDGE,"E511")}),1.0]])]});
            extrude(context, id + "F42", {"entities" : qUnion([Q0, Q1]), "depth" : 3 * mm});
        }
        {
            var Q0;
            Q0=makeQuery(id+"F8.imprint","IMPRINT",FACE,{"disambiguationData":[TD([[makeQuery(id+"F8.imprint","IMPRINT",EDGE,{"derivedFrom":sQuery(id+"F8.wireOp",EDGE,"E511")}),1.0]])]});
            extrude(context, id + "F43", {"entities" : qUnion([Q0]), "operationType" : NewBodyOperationType.ADD, "depth" : 13 * mm});
        }
        {
            var Q0;
            Q0=qCreatedBy(makeId("Top.planeOp"),FACE);
            var sketch = newSketch(context, id + "F44", { "sketchPlane" : qUnion([Q0])});
            skCircle(sketch, "E545.cCircle", {"center": v(34.4, 43.98) * mm, "radius": 5 * mm, "construction": true});
            skLineSegment(sketch, "E545.0", {"start": v(39.32, 40.96) * mm, "end": v(34.24, 38.21) * mm});
            skLineSegment(sketch, "E545.1", {"start": v(34.24, 38.21) * mm, "end": v(29.33, 41.24) * mm});
            skLineSegment(sketch, "E545.2", {"start": v(29.33, 41.24) * mm, "end": v(29.49, 47) * mm});
            skLineSegment(sketch, "E545.3", {"start": v(29.49, 47) * mm, "end": v(34.56, 49.75) * mm});
            skLineSegment(sketch, "E545.4", {"start": v(34.56, 49.75) * mm, "end": v(39.48, 46.73) * mm});
            skLineSegment(sketch, "E545.5", {"start": v(39.48, 46.73) * mm, "end": v(39.32, 40.96) * mm});
            skPoint(sketch, "E545.0.midPoint", {"position": v(36.78, 39.59) * mm});
            skCircle(sketch, "E546", {"center": v(34.4, 43.98) * mm, "radius": 3 * mm});
            skCircle(sketch, "E547", {"center": v(34.4, 43.98) * mm, "radius": 4.07 * mm});
            skSolve(sketch);
        }
        {
            var Q0;
            Q0=makeQuery(id+"F44.imprint","IMPRINT",FACE,{"disambiguationData":[TD([[makeQuery(id+"F44.imprint","IMPRINT",EDGE,{"derivedFrom":sQuery(id+"F44.wireOp",EDGE,"E546")}),-1.0]])]});
            var Q1;
            Q1=makeQuery(id+"F44.imprint","IMPRINT",FACE,{"disambiguationData":[TD([[makeQuery(id+"F44.imprint","IMPRINT",EDGE,{"derivedFrom":sQuery(id+"F44.wireOp",EDGE,"E545.0")}),-1.0]])]});
            extrude(context, id + "F45", {"entities" : qUnion([Q0, Q1]), "depth" : 5 * mm});
        }
        {
            var Q0;
            Q0=makeQuery(id+"F44.imprint","IMPRINT",FACE,{"disambiguationData":[TD([[makeQuery(id+"F44.imprint","IMPRINT",EDGE,{"derivedFrom":sQuery(id+"F44.wireOp",EDGE,"E546")}),-1.0]])]});
            extrude(context, id + "F46", {"entities" : qUnion([Q0]), "operationType" : NewBodyOperationType.ADD, "depth" : 7 * mm});
        }
        {
            var Q0;
            Q0=makeQuery(id+"F46.opExtrude","CAP_EDGE",EDGE,{"disambiguationData":[OSD([sQuery(id+"F44.wireOp",EDGE,"E547")])],"isStart":false});
            fillet(context, id + "F47", {"entities" : qUnion([Q0]), "radius" : 1 * mm, "tangentPropagation" : true, "allowEdgeOverflow" : false});
        }
    });
